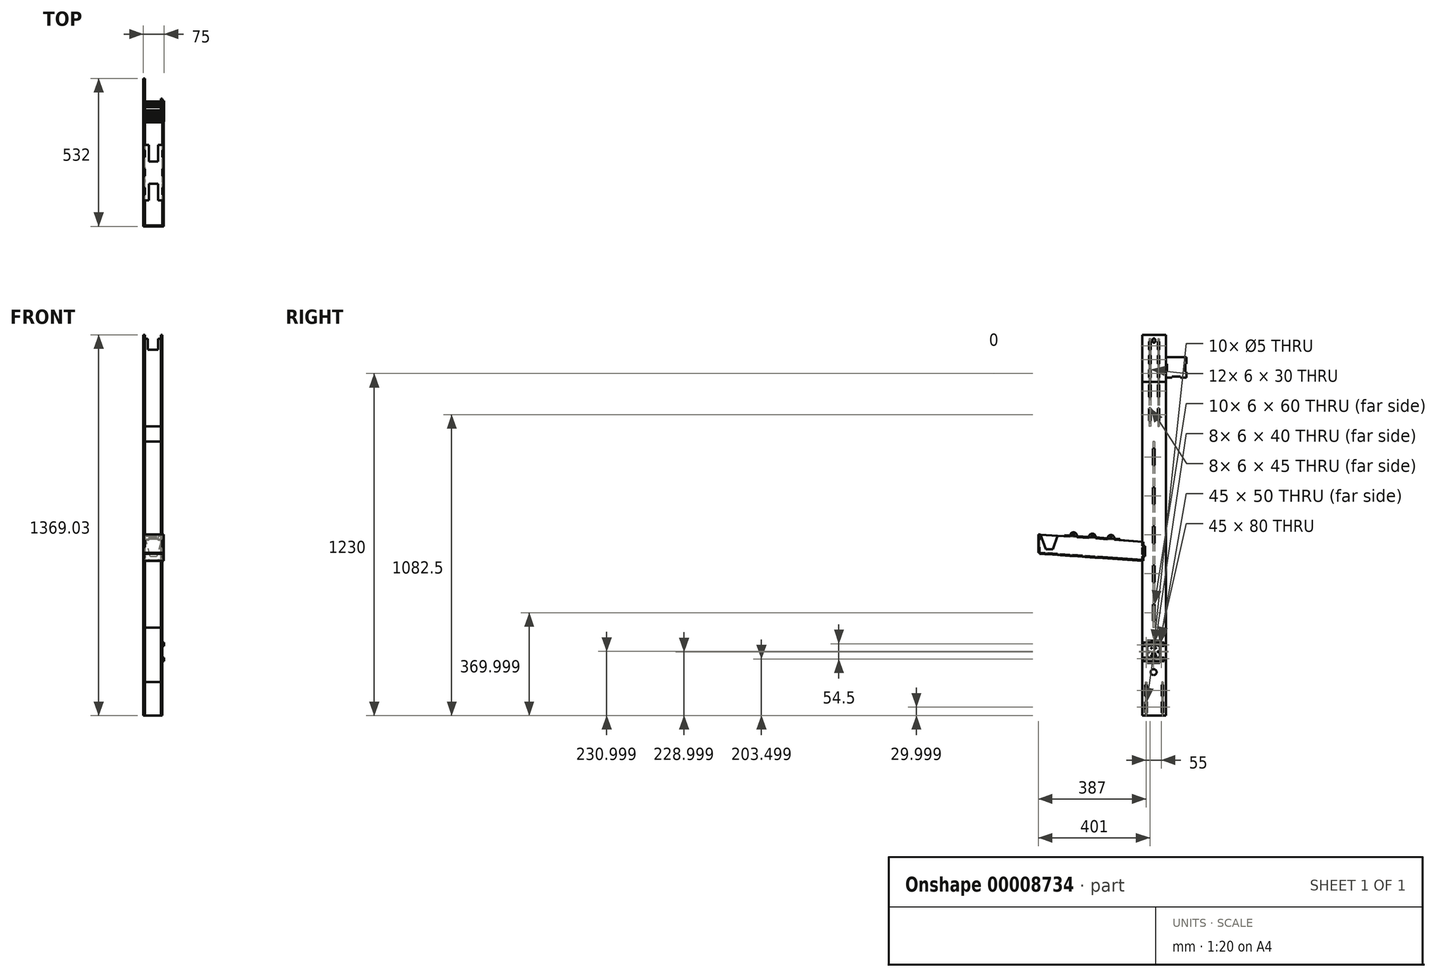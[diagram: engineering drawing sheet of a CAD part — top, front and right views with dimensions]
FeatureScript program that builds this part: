
annotation { "Feature Type Name" : "Feature", "Feature Type Description" : "" }
export const myFeature = defineFeature(function(context is Context, id is Id, definition is map)
    precondition{}
    {
        {
            var Q0;
            Q0=qCreatedBy(makeId("Right.planeOp"),FACE);
            cPlane(context, id + "F0", {"entities" : qUnion([Q0]), "cplaneType" : CPlaneType.OFFSET, "offset" : (65 / 2) * mm, "width" : 150 * mm, "height" : 150 * mm});
        }
        {
            var Q0;
            Q0=qCreatedBy(id+"F0.planeOp",FACE);
            var sketch = newSketch(context, id + "F1", { "sketchPlane" : qUnion([Q0])});
            skLineSegment(sketch, "E0", {"start": v(0, 0) * mm, "end": v(0, 0) * mm});
            skLineSegment(sketch, "E1", {"start": v(0, 65.16) * mm, "end": v(109.73, 57.49) * mm});
            skLineSegment(sketch, "E2", {"start": v(0, 0) * mm, "end": v(19.95, -1.4) * mm});
            skLineSegment(sketch, "E3", {"start": v(370, 39.29) * mm, "end": v(269.34, 46.32) * mm});
            skLineSegment(sketch, "E4", {"start": v(209.49, -14.65) * mm, "end": v(370, -25.87) * mm});
            skCircle(sketch, "E5", {"center": v(34, 62.78) * mm, "radius": 30 * mm, "construction": true});
            skLineSegment(sketch, "E6", {"start": v(64, 65.16) * mm, "end": v(64, -4.48) * mm, "construction": true});
            skLineSegment(sketch, "E7", {"start": v(0, 65.16) * mm, "end": v(64, 65.16) * mm, "construction": true});
            skLineSegment(sketch, "E8", {"start": v(0, 45) * mm, "end": v(0, 65.16) * mm});
            skLineSegment(sketch, "E9", {"start": v(0, 0) * mm, "end": v(0, 20) * mm});
            skLineSegment(sketch, "E10", {"start": v(199.51, -13.95) * mm, "end": v(199.23, -17.94) * mm});
            skLineSegment(sketch, "E11", {"start": v(209.2, -18.64) * mm, "end": v(199.23, -17.94) * mm});
            skLineSegment(sketch, "E12", {"start": v(209.2, -18.64) * mm, "end": v(209.49, -14.65) * mm});
            skLineSegment(sketch, "E13", {"start": v(109.73, -7.67) * mm, "end": v(109.45, -11.66) * mm});
            skLineSegment(sketch, "E14", {"start": v(109.45, -11.66) * mm, "end": v(119.43, -12.36) * mm});
            skLineSegment(sketch, "E15", {"start": v(119.43, -12.36) * mm, "end": v(119.7, -8.37) * mm});
            skLineSegment(sketch, "E16", {"start": v(164.6, -11.5) * mm, "end": v(164.32, -15.5) * mm});
            skLineSegment(sketch, "E17", {"start": v(164.32, -15.5) * mm, "end": v(154.34, -14.8) * mm});
            skLineSegment(sketch, "E18", {"start": v(154.34, -14.8) * mm, "end": v(154.62, -10.81) * mm});
            skLineSegment(sketch, "E19.trimOffspring", {"start": v(164.6, -11.5) * mm, "end": v(199.51, -13.95) * mm});
            skLineSegment(sketch, "E20.trimOffspring", {"start": v(119.7, -8.37) * mm, "end": v(154.62, -10.81) * mm});
            skLineSegment(sketch, "E21", {"start": v(74.82, -5.23) * mm, "end": v(74.54, -9.22) * mm});
            skLineSegment(sketch, "E22", {"start": v(74.54, -9.22) * mm, "end": v(64.56, -8.52) * mm});
            skLineSegment(sketch, "E23", {"start": v(64.56, -8.52) * mm, "end": v(64.84, -4.53) * mm});
            skLineSegment(sketch, "E24", {"start": v(29.93, -2.1) * mm, "end": v(29.65, -6.08) * mm});
            skLineSegment(sketch, "E25", {"start": v(29.65, -6.08) * mm, "end": v(19.67, -5.39) * mm});
            skLineSegment(sketch, "E26", {"start": v(19.67, -5.39) * mm, "end": v(19.95, -1.4) * mm});
            skLineSegment(sketch, "E27.trimOffspring", {"start": v(74.82, -5.23) * mm, "end": v(109.73, -7.67) * mm});
            skLineSegment(sketch, "E28.trimOffspring", {"start": v(29.93, -2.1) * mm, "end": v(64.84, -4.53) * mm});
            skLineSegment(sketch, "E29", {"start": v(269.34, 46.32) * mm, "end": v(269.62, 50.31) * mm});
            skLineSegment(sketch, "E30", {"start": v(269.62, 50.31) * mm, "end": v(244.68, 52.06) * mm, "construction": true});
            skLineSegment(sketch, "E31", {"start": v(244.68, 52.06) * mm, "end": v(244.4, 48.07) * mm});
            skLineSegment(sketch, "E32", {"start": v(202, 51.03) * mm, "end": v(202.29, 55.02) * mm});
            skLineSegment(sketch, "E33", {"start": v(202.29, 55.02) * mm, "end": v(177.35, 56.77) * mm, "construction": true});
            skLineSegment(sketch, "E34", {"start": v(177.35, 56.77) * mm, "end": v(177.07, 52.78) * mm});
            skLineSegment(sketch, "E35", {"start": v(134.67, 55.74) * mm, "end": v(134.95, 59.73) * mm});
            skLineSegment(sketch, "E36", {"start": v(134.95, 59.73) * mm, "end": v(110.01, 61.48) * mm, "construction": true});
            skLineSegment(sketch, "E37", {"start": v(110.01, 61.48) * mm, "end": v(109.73, 57.49) * mm});
            skLineSegment(sketch, "E38.trimOffspring", {"start": v(202, 51.03) * mm, "end": v(244.4, 48.07) * mm});
            skLineSegment(sketch, "E39.trimOffspring", {"start": v(134.67, 55.74) * mm, "end": v(177.07, 52.78) * mm});
            skArc(sketch, "E40", {"start": v(269.62, 50.31) * mm, "mid": v(258.02, 63.66) * mm, "end": v(244.68, 52.06) * mm});
            skArc(sketch, "E41", {"start": v(202.29, 55.02) * mm, "mid": v(190.69, 68.36) * mm, "end": v(177.35, 56.77) * mm});
            skArc(sketch, "E42", {"start": v(134.95, 59.73) * mm, "mid": v(123.35, 73.07) * mm, "end": v(110.01, 61.48) * mm});
            skLineSegment(sketch, "E43", {"start": v(257.15, 51.19) * mm, "end": v(258.02, 63.66) * mm, "construction": true});
            skLineSegment(sketch, "E44", {"start": v(189.82, 55.9) * mm, "end": v(190.69, 68.36) * mm, "construction": true});
            skLineSegment(sketch, "E45", {"start": v(122.48, 60.6) * mm, "end": v(123.35, 73.07) * mm, "construction": true});
            skCircle(sketch, "E46", {"center": v(190.3, 62.88) * mm, "radius": 3 * mm});
            skCircle(sketch, "E47", {"center": v(122.97, 67.59) * mm, "radius": 3 * mm});
            skLineSegment(sketch, "E48", {"start": v(257.85, 61.16) * mm, "end": v(123.18, 70.58) * mm, "construction": true});
            skCircle(sketch, "E49", {"center": v(257.64, 58.17) * mm, "radius": 3 * mm});
            skLineSegment(sketch, "E50", {"start": v(0, 45) * mm, "end": v(-4, 45) * mm});
            skLineSegment(sketch, "E51", {"start": v(-4, 45) * mm, "end": v(-4, 20) * mm});
            skLineSegment(sketch, "E52", {"start": v(-4, 20) * mm, "end": v(0, 20) * mm});
            skLineSegment(sketch, "E53.bottom", {"start": v(374, -6.87) * mm, "end": v(370, -6.87) * mm});
            skLineSegment(sketch, "E53.top", {"start": v(374, 15.13) * mm, "end": v(370, 15.13) * mm});
            skLineSegment(sketch, "E53.left", {"start": v(374, -6.87) * mm, "end": v(374, 15.13) * mm});
            skLineSegment(sketch, "E53.right", {"start": v(370, -6.87) * mm, "end": v(370, 15.13) * mm});
            skLineSegment(sketch, "E54", {"start": v(455, 614.16) * mm, "end": v(455, -585.84) * mm});
            skLineSegment(sketch, "E55", {"start": v(455, -585.84) * mm, "end": v(370, -585.84) * mm});
            skLineSegment(sketch, "E56", {"start": v(370, -585.84) * mm, "end": v(370, -25.87) * mm});
            skLineSegment(sketch, "E57", {"start": v(455, 614.16) * mm, "end": v(370, 614.16) * mm});
            skLineSegment(sketch, "E58", {"start": v(370, 614.16) * mm, "end": v(370, 39.29) * mm});
            skCircle(sketch, "E59", {"center": v(410.5, -429.84) * mm, "radius": 32.5 * mm, "construction": true});
            skCircle(sketch, "E60", {"center": v(410.5, 765.16) * mm, "radius": 32.5 * mm, "construction": true});
            skCircle(sketch, "E61", {"center": v(410.5, -429.84) * mm, "radius": 10.75 * mm});
            skLineSegment(sketch, "E62.bottom", {"start": v(445, -575.84) * mm, "end": v(439, -575.84) * mm});
            skLineSegment(sketch, "E62.top", {"start": v(445, -535.84) * mm, "end": v(439, -535.84) * mm});
            skLineSegment(sketch, "E62.left", {"start": v(445, -575.84) * mm, "end": v(445, -535.84) * mm});
            skLineSegment(sketch, "E62.right", {"start": v(439, -575.84) * mm, "end": v(439, -535.84) * mm});
            skLineSegment(sketch, "E63.bottom", {"start": v(445, -515.84) * mm, "end": v(439, -515.84) * mm});
            skLineSegment(sketch, "E63.top", {"start": v(445, -475.84) * mm, "end": v(439, -475.84) * mm});
            skLineSegment(sketch, "E63.left", {"start": v(445, -515.84) * mm, "end": v(445, -475.84) * mm});
            skLineSegment(sketch, "E63.right", {"start": v(439, -515.84) * mm, "end": v(439, -475.84) * mm});
            skLineSegment(sketch, "E64.bottom", {"start": v(386, -475.84) * mm, "end": v(380, -475.84) * mm});
            skLineSegment(sketch, "E64.top", {"start": v(386, -515.84) * mm, "end": v(380, -515.84) * mm});
            skLineSegment(sketch, "E64.left", {"start": v(386, -475.84) * mm, "end": v(386, -515.84) * mm});
            skLineSegment(sketch, "E64.right", {"start": v(380, -475.84) * mm, "end": v(380, -515.84) * mm});
            skLineSegment(sketch, "E65.bottom", {"start": v(386, -535.84) * mm, "end": v(380, -535.84) * mm});
            skLineSegment(sketch, "E65.top", {"start": v(386, -575.84) * mm, "end": v(380, -575.84) * mm});
            skLineSegment(sketch, "E65.left", {"start": v(386, -535.84) * mm, "end": v(386, -575.84) * mm});
            skLineSegment(sketch, "E65.right", {"start": v(380, -535.84) * mm, "end": v(380, -575.84) * mm});
            skLineSegment(sketch, "E66.bottom", {"start": v(431, 604.16) * mm, "end": v(425, 604.16) * mm});
            skLineSegment(sketch, "E66.top", {"start": v(431, 559.16) * mm, "end": v(425, 559.16) * mm});
            skLineSegment(sketch, "E66.left", {"start": v(431, 604.16) * mm, "end": v(431, 559.16) * mm});
            skLineSegment(sketch, "E66.right", {"start": v(425, 604.16) * mm, "end": v(425, 559.16) * mm});
            skLineSegment(sketch, "E67.bottom", {"start": v(431, 519.16) * mm, "end": v(425, 519.16) * mm});
            skLineSegment(sketch, "E67.top", {"start": v(431, 474.16) * mm, "end": v(425, 474.16) * mm});
            skLineSegment(sketch, "E67.left", {"start": v(431, 519.16) * mm, "end": v(431, 474.16) * mm});
            skLineSegment(sketch, "E67.right", {"start": v(425, 519.16) * mm, "end": v(425, 474.16) * mm});
            skLineSegment(sketch, "E68.bottom", {"start": v(400, 604.16) * mm, "end": v(394, 604.16) * mm});
            skLineSegment(sketch, "E68.top", {"start": v(400, 559.16) * mm, "end": v(394, 559.16) * mm});
            skLineSegment(sketch, "E68.left", {"start": v(400, 604.16) * mm, "end": v(400, 559.16) * mm});
            skLineSegment(sketch, "E68.right", {"start": v(394, 604.16) * mm, "end": v(394, 559.16) * mm});
            skLineSegment(sketch, "E69.bottom", {"start": v(400, 519.16) * mm, "end": v(394, 519.16) * mm});
            skLineSegment(sketch, "E69.top", {"start": v(400, 474.16) * mm, "end": v(394, 474.16) * mm});
            skLineSegment(sketch, "E69.left", {"start": v(400, 519.16) * mm, "end": v(400, 474.16) * mm});
            skLineSegment(sketch, "E69.right", {"start": v(394, 519.16) * mm, "end": v(394, 474.16) * mm});
            skLineSegment(sketch, "E70", {"start": v(425, 604.16) * mm, "end": v(400, 604.16) * mm, "construction": true});
            skLineSegment(sketch, "E71", {"start": v(412.5, 604.16) * mm, "end": v(412.5, 614.16) * mm, "construction": true});
            skLineSegment(sketch, "E72.bottom", {"start": v(433, -329.84) * mm, "end": v(388, -329.84) * mm});
            skLineSegment(sketch, "E72.top", {"start": v(433, -379.84) * mm, "end": v(388, -379.84) * mm});
            skLineSegment(sketch, "E72.left", {"start": v(433, -329.84) * mm, "end": v(433, -379.84) * mm});
            skLineSegment(sketch, "E72.right", {"start": v(388, -329.84) * mm, "end": v(388, -379.84) * mm});
            skPoint(sketch, "E73", {"position": v(410.5, -329.84) * mm});
            skLineSegment(sketch, "E74.bottom", {"start": v(413.5, -245.84) * mm, "end": v(407.5, -245.84) * mm});
            skLineSegment(sketch, "E74.top", {"start": v(413.5, -185.84) * mm, "end": v(407.5, -185.84) * mm});
            skLineSegment(sketch, "E74.left", {"start": v(413.5, -245.84) * mm, "end": v(413.5, -185.84) * mm});
            skLineSegment(sketch, "E74.right", {"start": v(407.5, -245.84) * mm, "end": v(407.5, -185.84) * mm});
            skLineSegment(sketch, "E75.bottom", {"start": v(413.5, -105.84) * mm, "end": v(407.5, -105.84) * mm});
            skLineSegment(sketch, "E75.top", {"start": v(413.5, -45.84) * mm, "end": v(407.5, -45.84) * mm});
            skLineSegment(sketch, "E75.left", {"start": v(413.5, -105.84) * mm, "end": v(413.5, -45.84) * mm});
            skLineSegment(sketch, "E75.right", {"start": v(407.5, -105.84) * mm, "end": v(407.5, -45.84) * mm});
            skLineSegment(sketch, "E76.bottom", {"start": v(413.5, 34.16) * mm, "end": v(407.5, 34.16) * mm});
            skLineSegment(sketch, "E76.top", {"start": v(413.5, 94.16) * mm, "end": v(407.5, 94.16) * mm});
            skLineSegment(sketch, "E76.left", {"start": v(413.5, 34.16) * mm, "end": v(413.5, 94.16) * mm});
            skLineSegment(sketch, "E76.right", {"start": v(407.5, 34.16) * mm, "end": v(407.5, 94.16) * mm});
            skLineSegment(sketch, "E77.bottom", {"start": v(413.5, 174.16) * mm, "end": v(407.5, 174.16) * mm});
            skLineSegment(sketch, "E77.top", {"start": v(413.5, 234.16) * mm, "end": v(407.5, 234.16) * mm});
            skLineSegment(sketch, "E77.left", {"start": v(413.5, 174.16) * mm, "end": v(413.5, 234.16) * mm});
            skLineSegment(sketch, "E77.right", {"start": v(407.5, 174.16) * mm, "end": v(407.5, 234.16) * mm});
            skLineSegment(sketch, "E78.bottom", {"start": v(413.5, 314.16) * mm, "end": v(407.5, 314.16) * mm});
            skLineSegment(sketch, "E78.top", {"start": v(413.5, 374.16) * mm, "end": v(407.5, 374.16) * mm});
            skLineSegment(sketch, "E78.left", {"start": v(413.5, 314.16) * mm, "end": v(413.5, 374.16) * mm});
            skLineSegment(sketch, "E78.right", {"start": v(407.5, 314.16) * mm, "end": v(407.5, 374.16) * mm});
            skLineSegment(sketch, "E79", {"start": v(413.5, -185.84) * mm, "end": v(413.5, -105.84) * mm, "construction": true});
            skLineSegment(sketch, "E80", {"start": v(413.5, -45.84) * mm, "end": v(413.5, 34.16) * mm, "construction": true});
            skLineSegment(sketch, "E81", {"start": v(413.5, 94.16) * mm, "end": v(413.5, 174.16) * mm, "construction": true});
            skLineSegment(sketch, "E82", {"start": v(413.5, 314.16) * mm, "end": v(413.5, 234.16) * mm, "construction": true});
            skPoint(sketch, "E83", {"position": v(410.5, -245.84) * mm});
            skSolve(sketch);
        }
        {
            var Q0;
            Q0 = qSketchRegion(id + "F1", true);
            extrude(context, id + "F2", {"entities" : qUnion([Q0]), "depth" : 4 * mm, "hasSecondDirection" : true, "secondDirectionOppositeDirection" : true, "secondDirectionDepth" : 2 * mm});
        }
        {
            var Q0;
            Q0=makeQuery(id+"F2.opExtrude","SWEPT_FACE",FACE,{"disambiguationData":[OSD([sQuery(id+"F1.wireOp",EDGE,"E2")])]});
            var sketch = newSketch(context, id + "F3", { "sketchPlane" : qUnion([Q0])});
            skLineSegment(sketch, "E84.bottom", {"start": v(30.5, 0) * mm, "end": v(103.5, 0) * mm});
            skLineSegment(sketch, "E84.top", {"start": v(30.5, -370.91) * mm, "end": v(47.5, -370.91) * mm});
            skLineSegment(sketch, "E84.left", {"start": v(30.5, 0) * mm, "end": v(30.5, -20) * mm});
            skLineSegment(sketch, "E84.right", {"start": v(103.5, 0) * mm, "end": v(103.5, -20) * mm});
            skLineSegment(sketch, "E85", {"start": v(88.5, -370.91) * mm, "end": v(88.5, -374.91) * mm});
            skLineSegment(sketch, "E86", {"start": v(47.5, -374.91) * mm, "end": v(47.5, -370.91) * mm});
            skLineSegment(sketch, "E87", {"start": v(82.5, -370.91) * mm, "end": v(82.5, -374.91) * mm});
            skLineSegment(sketch, "E88", {"start": v(53.5, -374.91) * mm, "end": v(53.5, -370.91) * mm});
            skLineSegment(sketch, "E89.trimOffspring", {"start": v(88.5, -370.91) * mm, "end": v(103.5, -370.91) * mm});
            skLineSegment(sketch, "E90.trimOffspring", {"start": v(53.5, -370.91) * mm, "end": v(82.5, -370.91) * mm});
            skLineSegment(sketch, "E91.0.1", {"start": v(30.5, -30) * mm, "end": v(36.5, -30) * mm});
            skLineSegment(sketch, "E91.0.2", {"start": v(36.5, -30) * mm, "end": v(36.5, -20) * mm});
            skLineSegment(sketch, "E91.0.3", {"start": v(36.5, -20) * mm, "end": v(30.5, -20) * mm});
            skLineSegment(sketch, "E91.1.1", {"start": v(30.5, -75) * mm, "end": v(36.5, -75) * mm});
            skLineSegment(sketch, "E91.1.2", {"start": v(36.5, -75) * mm, "end": v(36.5, -65) * mm});
            skLineSegment(sketch, "E91.1.3", {"start": v(36.5, -65) * mm, "end": v(30.5, -65) * mm});
            skLineSegment(sketch, "E91.2.1", {"start": v(30.5, -120) * mm, "end": v(36.5, -120) * mm});
            skLineSegment(sketch, "E91.2.2", {"start": v(36.5, -120) * mm, "end": v(36.5, -110) * mm});
            skLineSegment(sketch, "E91.2.3", {"start": v(36.5, -110) * mm, "end": v(30.5, -110) * mm});
            skLineSegment(sketch, "E91.3.1", {"start": v(30.5, -210) * mm, "end": v(36.5, -210) * mm});
            skLineSegment(sketch, "E91.3.2", {"start": v(36.5, -210) * mm, "end": v(36.5, -200) * mm});
            skLineSegment(sketch, "E91.3.3", {"start": v(36.5, -200) * mm, "end": v(30.5, -200) * mm});
            skLineSegment(sketch, "E91.4.1", {"start": v(30.5, -165) * mm, "end": v(36.5, -165) * mm});
            skLineSegment(sketch, "E91.4.2", {"start": v(36.5, -165) * mm, "end": v(36.5, -155) * mm});
            skLineSegment(sketch, "E91.4.3", {"start": v(36.5, -155) * mm, "end": v(30.5, -155) * mm});
            skLineSegment(sketch, "E92.trimOffspring", {"start": v(30.5, -165) * mm, "end": v(30.5, -200) * mm});
            skLineSegment(sketch, "E93.trimOffspring", {"start": v(30.5, -210) * mm, "end": v(30.5, -370.91) * mm});
            skLineSegment(sketch, "E94.trimOffspring", {"start": v(30.5, -120) * mm, "end": v(30.5, -155) * mm});
            skLineSegment(sketch, "E95.trimOffspring", {"start": v(30.5, -75) * mm, "end": v(30.5, -110) * mm});
            skLineSegment(sketch, "E96.trimOffspring", {"start": v(30.5, -30) * mm, "end": v(30.5, -65) * mm});
            skLineSegment(sketch, "E97.bottom", {"start": v(103.5, -20) * mm, "end": v(99.5, -20) * mm});
            skLineSegment(sketch, "E97.top", {"start": v(103.5, -30) * mm, "end": v(99.5, -30) * mm});
            skLineSegment(sketch, "E97.right", {"start": v(99.5, -20) * mm, "end": v(99.5, -30) * mm});
            skLineSegment(sketch, "E98.bottom", {"start": v(103.5, -65) * mm, "end": v(99.5, -65) * mm});
            skLineSegment(sketch, "E98.top", {"start": v(103.5, -75) * mm, "end": v(99.5, -75) * mm});
            skLineSegment(sketch, "E98.right", {"start": v(99.5, -65) * mm, "end": v(99.5, -75) * mm});
            skLineSegment(sketch, "E99.bottom", {"start": v(103.5, -110) * mm, "end": v(99.5, -110) * mm});
            skLineSegment(sketch, "E99.top", {"start": v(103.5, -120) * mm, "end": v(99.5, -120) * mm});
            skLineSegment(sketch, "E99.right", {"start": v(99.5, -110) * mm, "end": v(99.5, -120) * mm});
            skLineSegment(sketch, "E100.bottom", {"start": v(103.5, -155) * mm, "end": v(99.5, -155) * mm});
            skLineSegment(sketch, "E100.top", {"start": v(103.5, -165) * mm, "end": v(99.5, -165) * mm});
            skLineSegment(sketch, "E100.right", {"start": v(99.5, -155) * mm, "end": v(99.5, -165) * mm});
            skLineSegment(sketch, "E101.bottom", {"start": v(103.5, -200) * mm, "end": v(99.5, -200) * mm});
            skLineSegment(sketch, "E101.top", {"start": v(103.5, -210) * mm, "end": v(99.5, -210) * mm});
            skLineSegment(sketch, "E101.right", {"start": v(99.5, -200) * mm, "end": v(99.5, -210) * mm});
            skLineSegment(sketch, "E102.trimOffspring", {"start": v(103.5, -210) * mm, "end": v(103.5, -370.91) * mm});
            skLineSegment(sketch, "E103.trimOffspring", {"start": v(103.5, -165) * mm, "end": v(103.5, -200) * mm});
            skLineSegment(sketch, "E104.trimOffspring", {"start": v(103.5, -120) * mm, "end": v(103.5, -155) * mm});
            skLineSegment(sketch, "E105.trimOffspring", {"start": v(103.5, -75) * mm, "end": v(103.5, -110) * mm});
            skLineSegment(sketch, "E106.trimOffspring", {"start": v(103.5, -30) * mm, "end": v(103.5, -65) * mm});
            skLineSegment(sketch, "E107", {"start": v(82.5, -374.91) * mm, "end": v(88.5, -374.91) * mm});
            skLineSegment(sketch, "E108", {"start": v(47.5, -374.91) * mm, "end": v(53.5, -374.91) * mm});
            skSolve(sketch);
        }
        {
            var Q0;
            Q0 = qSketchRegion(id + "F3", true);
            extrude(context, id + "F4", {"entities" : qUnion([Q0]), "depth" : 4 * mm});
        }
        {
            var Q0;
            Q0=makeQuery(id+"F2.opExtrude","SWEPT_FACE",FACE,{"disambiguationData":[OSD([sQuery(id+"F1.wireOp",EDGE,"E9")])]});
            var sketch = newSketch(context, id + "F5", { "sketchPlane" : qUnion([Q0])});
            skLineSegment(sketch, "E109.bottom", {"start": v(30.5, 0) * mm, "end": v(103.5, 0) * mm});
            skLineSegment(sketch, "E109.top", {"start": v(32.5, 65.16) * mm, "end": v(103.5, 65.16) * mm});
            skLineSegment(sketch, "E110.0", {"start": v(36.5, 45) * mm, "end": v(32.5, 45) * mm});
            skLineSegment(sketch, "E110.1", {"start": v(36.5, 45) * mm, "end": v(36.5, 20) * mm});
            skLineSegment(sketch, "E110.2", {"start": v(36.5, 0) * mm, "end": v(30.5, 0) * mm});
            skLineSegment(sketch, "E110.3.1", {"start": v(30.5, 0) * mm, "end": v(36.5, 0) * mm});
            skLineSegment(sketch, "E110.3.2", {"start": v(36.5, 20) * mm, "end": v(36.5, 45) * mm});
            skLineSegment(sketch, "E110.3.3", {"start": v(36.5, 45) * mm, "end": v(32.5, 45) * mm});
            skLineSegment(sketch, "E111.trimOffspring", {"start": v(32.5, 45) * mm, "end": v(32.5, 65.16) * mm});
            skLineSegment(sketch, "E112.trimOffspring", {"start": v(30.5, 0) * mm, "end": v(30.5, 0) * mm});
            skLineSegment(sketch, "E113.bottom", {"start": v(103.5, 45) * mm, "end": v(99.5, 45) * mm});
            skLineSegment(sketch, "E113.top", {"start": v(103.5, 20) * mm, "end": v(99.5, 20) * mm});
            skLineSegment(sketch, "E113.right", {"start": v(99.5, 45) * mm, "end": v(99.5, 20) * mm});
            skLineSegment(sketch, "E114.trimOffspring", {"start": v(103.5, 0) * mm, "end": v(103.5, 20) * mm});
            skLineSegment(sketch, "E115.trimOffspring", {"start": v(103.5, 45) * mm, "end": v(103.5, 65.16) * mm});
            skLineSegment(sketch, "E116", {"start": v(36.5, 20) * mm, "end": v(30.5, 20) * mm});
            skLineSegment(sketch, "E117", {"start": v(30.5, 0) * mm, "end": v(30.5, 20) * mm});
            skSolve(sketch);
        }
        {
            var Q0;
            Q0 = qSketchRegion(id + "F5", true);
            extrude(context, id + "F6", {"entities" : qUnion([Q0]), "depth" : 4 * mm});
        }
        {
            var Q0;
            Q0=makeQuery(id+"F4.opExtrude","SWEPT_FACE",FACE,{"disambiguationData":[OSD([sQuery(id+"F3.wireOp",EDGE,"E84.right")])]});
            var sketch = newSketch(context, id + "F7", { "sketchPlane" : qUnion([Q0])});
            skLineSegment(sketch, "E118", {"start": v(370, -25.87) * mm, "end": v(370, -12.71) * mm});
            skLineSegment(sketch, "E119", {"start": v(370, 39.29) * mm, "end": v(269.34, 46.32) * mm});
            skLineSegment(sketch, "E120.bottom", {"start": v(370, 24.29) * mm, "end": v(380, 24.29) * mm});
            skLineSegment(sketch, "E120.top", {"start": v(370, -12.71) * mm, "end": v(380, -12.71) * mm});
            skLineSegment(sketch, "E120.right", {"start": v(380, 24.29) * mm, "end": v(380, -12.71) * mm});
            skLineSegment(sketch, "E121", {"start": v(370, 18.29) * mm, "end": v(374, 18.29) * mm});
            skLineSegment(sketch, "E122", {"start": v(374, 18.29) * mm, "end": v(374, -6.71) * mm});
            skLineSegment(sketch, "E123", {"start": v(374, -6.71) * mm, "end": v(370, -6.71) * mm});
            skLineSegment(sketch, "E124.trimOffspring", {"start": v(370, 24.29) * mm, "end": v(370, 39.29) * mm});
            skLineSegment(sketch, "E125.trimOffspring", {"start": v(370, -6.71) * mm, "end": v(370, 18.29) * mm});
            skLineSegment(sketch, "E126", {"start": v(0, 45) * mm, "end": v(-4, 45) * mm});
            skLineSegment(sketch, "E127", {"start": v(-4, 45) * mm, "end": v(-4, 20) * mm});
            skLineSegment(sketch, "E128", {"start": v(-4, 20) * mm, "end": v(0, 20) * mm});
            skLineSegment(sketch, "E129.trimOffspring", {"start": v(0, 0) * mm, "end": v(0, 20) * mm});
            skLineSegment(sketch, "E130.0", {"start": v(29.93, -2.1) * mm, "end": v(29.65, -6.08) * mm});
            skLineSegment(sketch, "E130.1", {"start": v(19.67, -5.39) * mm, "end": v(19.95, -1.4) * mm});
            skLineSegment(sketch, "E130.2", {"start": v(29.65, -6.08) * mm, "end": v(19.67, -5.39) * mm});
            skLineSegment(sketch, "E130.3", {"start": v(64.56, -8.52) * mm, "end": v(64.84, -4.53) * mm});
            skLineSegment(sketch, "E130.4", {"start": v(74.54, -9.22) * mm, "end": v(64.56, -8.52) * mm});
            skLineSegment(sketch, "E130.5", {"start": v(74.82, -5.23) * mm, "end": v(74.54, -9.22) * mm});
            skLineSegment(sketch, "E130.6", {"start": v(109.73, -7.67) * mm, "end": v(109.45, -11.66) * mm});
            skLineSegment(sketch, "E130.7", {"start": v(119.43, -12.36) * mm, "end": v(119.7, -8.37) * mm});
            skLineSegment(sketch, "E130.8", {"start": v(109.45, -11.66) * mm, "end": v(119.43, -12.36) * mm});
            skLineSegment(sketch, "E130.9", {"start": v(74.82, -5.23) * mm, "end": v(109.73, -7.67) * mm});
            skLineSegment(sketch, "E130.10", {"start": v(29.93, -2.1) * mm, "end": v(64.84, -4.53) * mm});
            skLineSegment(sketch, "E130.11", {"start": v(0, 0) * mm, "end": v(19.95, -1.4) * mm});
            skLineSegment(sketch, "E130.12", {"start": v(119.7, -8.37) * mm, "end": v(154.62, -10.81) * mm});
            skLineSegment(sketch, "E130.13", {"start": v(154.34, -14.8) * mm, "end": v(154.62, -10.81) * mm});
            skLineSegment(sketch, "E130.14", {"start": v(164.32, -15.5) * mm, "end": v(154.34, -14.8) * mm});
            skLineSegment(sketch, "E130.15", {"start": v(164.6, -11.5) * mm, "end": v(164.32, -15.5) * mm});
            skLineSegment(sketch, "E130.16", {"start": v(164.6, -11.5) * mm, "end": v(199.51, -13.95) * mm});
            skLineSegment(sketch, "E130.17", {"start": v(199.51, -13.95) * mm, "end": v(199.23, -17.94) * mm});
            skLineSegment(sketch, "E130.18", {"start": v(209.2, -18.64) * mm, "end": v(199.23, -17.94) * mm});
            skLineSegment(sketch, "E130.19", {"start": v(209.2, -18.64) * mm, "end": v(209.49, -14.65) * mm});
            skLineSegment(sketch, "E130.20", {"start": v(209.49, -14.65) * mm, "end": v(370, -25.87) * mm});
            skLineSegment(sketch, "E131", {"start": v(109.73, 57.49) * mm, "end": v(110.01, 61.48) * mm});
            skLineSegment(sketch, "E132", {"start": v(110.01, 61.48) * mm, "end": v(134.95, 59.73) * mm});
            skLineSegment(sketch, "E133", {"start": v(134.95, 59.73) * mm, "end": v(134.67, 55.74) * mm});
            skLineSegment(sketch, "E134.trimOffspring", {"start": v(109.73, 57.49) * mm, "end": v(65.13, 60.6) * mm});
            skLineSegment(sketch, "E135", {"start": v(177.07, 52.78) * mm, "end": v(177.35, 56.77) * mm});
            skLineSegment(sketch, "E136", {"start": v(177.35, 56.77) * mm, "end": v(202.29, 55.02) * mm});
            skLineSegment(sketch, "E137", {"start": v(202.29, 55.02) * mm, "end": v(202, 51.03) * mm});
            skLineSegment(sketch, "E138.trimOffspring", {"start": v(177.07, 52.78) * mm, "end": v(134.67, 55.74) * mm});
            skLineSegment(sketch, "E139", {"start": v(244.4, 48.07) * mm, "end": v(244.68, 52.06) * mm});
            skLineSegment(sketch, "E140", {"start": v(244.68, 52.06) * mm, "end": v(269.62, 50.31) * mm});
            skLineSegment(sketch, "E141", {"start": v(269.62, 50.31) * mm, "end": v(269.34, 46.32) * mm});
            skLineSegment(sketch, "E142.trimOffspring", {"start": v(244.4, 48.07) * mm, "end": v(202, 51.03) * mm});
            skLineSegment(sketch, "E143", {"start": v(0, 65.16) * mm, "end": v(0, 45) * mm});
            skLineSegment(sketch, "E144", {"start": v(4, 64.88) * mm, "end": v(22.96, 12.75) * mm});
            skLineSegment(sketch, "E145", {"start": v(22.96, 12.75) * mm, "end": v(47.71, 12.75) * mm});
            skLineSegment(sketch, "E146", {"start": v(47.71, 12.75) * mm, "end": v(65.13, 60.6) * mm});
            skLineSegment(sketch, "E147.trimOffspring", {"start": v(4, 64.88) * mm, "end": v(0, 65.16) * mm});
            skLineSegment(sketch, "E148", {"start": v(4, 64.88) * mm, "end": v(65.13, 60.6) * mm, "construction": true});
            skLineSegment(sketch, "E149", {"start": v(34.56, 62.74) * mm, "end": v(35.34, 12.75) * mm, "construction": true});
            skSolve(sketch);
        }
        {
            var Q0;
            Q0 = qSketchRegion(id + "F7", true);
            extrude(context, id + "F8", {"entities" : qUnion([Q0]), "oppositeDirection" : true, "depth" : 4 * mm});
        }
        {
            var Q0;
            Q0=makeQuery(id+"F8.opExtrude","SWEPT_FACE",FACE,{"disambiguationData":[OSD([sQuery(id+"F7.wireOp",EDGE,"E118")])]});
            var sketch = newSketch(context, id + "F9", { "sketchPlane" : qUnion([Q0])});
            skLineSegment(sketch, "E150.bottom", {"start": v(-103.5, 39.29) * mm, "end": v(-93.5, 39.29) * mm});
            skLineSegment(sketch, "E150.left", {"start": v(-103.5, 39.29) * mm, "end": v(-103.5, 24.29) * mm});
            skLineSegment(sketch, "E151.bottom", {"start": v(-103.5, 24.29) * mm, "end": v(-99.5, 24.29) * mm});
            skLineSegment(sketch, "E151.top", {"start": v(-103.5, 18.29) * mm, "end": v(-99.5, 18.29) * mm});
            skLineSegment(sketch, "E151.right", {"start": v(-99.5, 24.29) * mm, "end": v(-99.5, 18.29) * mm});
            skLineSegment(sketch, "E152.top", {"start": v(-103.5, -6.71) * mm, "end": v(-99.5, -6.71) * mm});
            skLineSegment(sketch, "E153.trimOffspring", {"start": v(-103.5, 18.29) * mm, "end": v(-103.5, -6.71) * mm});
            skLineSegment(sketch, "E154.trimOffspring", {"start": v(-41.5, 39.29) * mm, "end": v(-36.5, 39.29) * mm});
            skLineSegment(sketch, "E155", {"start": v(-99.5, -6.71) * mm, "end": v(-99.5, -12.71) * mm});
            skLineSegment(sketch, "E156", {"start": v(-99.5, -12.71) * mm, "end": v(-103.5, -12.71) * mm});
            skLineSegment(sketch, "E157", {"start": v(-103.5, -12.71) * mm, "end": v(-103.5, -29.86) * mm});
            skLineSegment(sketch, "E158", {"start": v(-103.5, -29.86) * mm, "end": v(-88.5, -29.86) * mm});
            skLineSegment(sketch, "E159", {"start": v(-88.5, -29.86) * mm, "end": v(-88.5, -25.87) * mm});
            skLineSegment(sketch, "E160", {"start": v(-88.5, -25.87) * mm, "end": v(-82.5, -25.87) * mm});
            skLineSegment(sketch, "E161", {"start": v(-82.5, -25.87) * mm, "end": v(-82.5, -29.86) * mm});
            skLineSegment(sketch, "E162", {"start": v(-82.5, -29.86) * mm, "end": v(-53.5, -29.86) * mm});
            skLineSegment(sketch, "E163", {"start": v(-53.5, -29.86) * mm, "end": v(-53.5, -25.87) * mm});
            skLineSegment(sketch, "E164", {"start": v(-53.5, -25.87) * mm, "end": v(-47.5, -25.87) * mm});
            skLineSegment(sketch, "E165", {"start": v(-47.5, -25.87) * mm, "end": v(-47.5, -29.86) * mm});
            skLineSegment(sketch, "E166", {"start": v(-47.5, -29.86) * mm, "end": v(-36.5, -29.86) * mm});
            skLineSegment(sketch, "E167", {"start": v(-93.5, 39.29) * mm, "end": v(-79, -14.86) * mm});
            skLineSegment(sketch, "E168", {"start": v(-79, -14.86) * mm, "end": v(-56, -14.86) * mm});
            skLineSegment(sketch, "E169", {"start": v(-56, -14.86) * mm, "end": v(-41.5, 39.29) * mm});
            skLineSegment(sketch, "E170", {"start": v(-36.5, 19.13) * mm, "end": v(-36.5, 15.13) * mm});
            skLineSegment(sketch, "E171", {"start": v(-36.5, 15.13) * mm, "end": v(-30.5, 15.13) * mm});
            skLineSegment(sketch, "E172", {"start": v(-30.5, -6.87) * mm, "end": v(-36.5, -6.87) * mm});
            skLineSegment(sketch, "E173", {"start": v(-36.5, -6.87) * mm, "end": v(-36.5, -10.88) * mm});
            skLineSegment(sketch, "E174.trimOffspring", {"start": v(-30.5, 15.13) * mm, "end": v(-30.5, -6.87) * mm});
            skLineSegment(sketch, "E175", {"start": v(-36.5, 19.13) * mm, "end": v(-36.5, 39.29) * mm});
            skLineSegment(sketch, "E176", {"start": v(-36.5, -10.88) * mm, "end": v(-36.5, -29.86) * mm});
            skLineSegment(sketch, "E177.bottom", {"start": v(-99.5, -1.71) * mm, "end": v(-93.5, -1.71) * mm});
            skLineSegment(sketch, "E177.top", {"start": v(-99.5, 13.29) * mm, "end": v(-93.5, 13.29) * mm});
            skLineSegment(sketch, "E177.left", {"start": v(-99.5, -1.71) * mm, "end": v(-99.5, 13.29) * mm});
            skLineSegment(sketch, "E177.right", {"start": v(-93.5, -1.71) * mm, "end": v(-93.5, 13.29) * mm});
            skSolve(sketch);
        }
        {
            var Q0;
            Q0 = qSketchRegion(id + "F9", true);
            extrude(context, id + "F10", {"entities" : qUnion([Q0]), "depth" : 4 * mm});
        }
        {
            var Q0;
            Q0=makeQuery(id+"F2.opExtrude","SWEPT_FACE",FACE,{"disambiguationData":[OSD([sQuery(id+"F1.wireOp",EDGE,"E1")])]});
            var sketch = newSketch(context, id + "F11", { "sketchPlane" : qUnion([Q0])});
            skLineSegment(sketch, "E178.bottom", {"start": v(30.5, 285.45) * mm, "end": v(50.5, 285.45) * mm});
            skLineSegment(sketch, "E178.top", {"start": v(30.5, 85.45) * mm, "end": v(50.5, 85.45) * mm});
            skLineSegment(sketch, "E178.right", {"start": v(103.5, 285.45) * mm, "end": v(103.5, 265.45) * mm});
            skLineSegment(sketch, "E179.top", {"start": v(50.5, 145.45) * mm, "end": v(83.5, 145.45) * mm});
            skLineSegment(sketch, "E179.left", {"start": v(50.5, 85.45) * mm, "end": v(50.5, 145.45) * mm});
            skLineSegment(sketch, "E179.right", {"start": v(83.5, 85.45) * mm, "end": v(83.5, 145.45) * mm});
            skLineSegment(sketch, "E180.top", {"start": v(50.5, 225.45) * mm, "end": v(83.5, 225.45) * mm});
            skLineSegment(sketch, "E180.left", {"start": v(50.5, 285.45) * mm, "end": v(50.5, 225.45) * mm});
            skLineSegment(sketch, "E180.right", {"start": v(83.5, 285.45) * mm, "end": v(83.5, 225.45) * mm});
            skLineSegment(sketch, "E181.trimOffspring", {"start": v(83.5, 85.45) * mm, "end": v(103.5, 85.45) * mm});
            skLineSegment(sketch, "E182.trimOffspring", {"start": v(83.5, 285.45) * mm, "end": v(103.5, 285.45) * mm});
            skLineSegment(sketch, "E183.bottom", {"start": v(30.5, 105.45) * mm, "end": v(36.5, 105.45) * mm});
            skLineSegment(sketch, "E183.top", {"start": v(30.5, 130.45) * mm, "end": v(36.5, 130.45) * mm});
            skLineSegment(sketch, "E183.right", {"start": v(36.5, 105.45) * mm, "end": v(36.5, 130.45) * mm});
            skLineSegment(sketch, "E184.bottom", {"start": v(103.5, 105.45) * mm, "end": v(99.5, 105.45) * mm});
            skLineSegment(sketch, "E184.top", {"start": v(103.5, 130.45) * mm, "end": v(99.5, 130.45) * mm});
            skLineSegment(sketch, "E184.right", {"start": v(99.5, 105.45) * mm, "end": v(99.5, 130.45) * mm});
            skLineSegment(sketch, "E185.bottom", {"start": v(36.5, 172.95) * mm, "end": v(30.5, 172.95) * mm});
            skLineSegment(sketch, "E185.top", {"start": v(36.5, 197.95) * mm, "end": v(30.5, 197.95) * mm});
            skLineSegment(sketch, "E185.left", {"start": v(36.5, 172.95) * mm, "end": v(36.5, 197.95) * mm});
            skLineSegment(sketch, "E186.bottom", {"start": v(30.5, 240.45) * mm, "end": v(36.5, 240.45) * mm});
            skLineSegment(sketch, "E186.top", {"start": v(30.5, 265.45) * mm, "end": v(36.5, 265.45) * mm});
            skLineSegment(sketch, "E186.right", {"start": v(36.5, 240.45) * mm, "end": v(36.5, 265.45) * mm});
            skLineSegment(sketch, "E187.bottom", {"start": v(99.5, 240.45) * mm, "end": v(103.5, 240.45) * mm});
            skLineSegment(sketch, "E187.top", {"start": v(99.5, 265.45) * mm, "end": v(103.5, 265.45) * mm});
            skLineSegment(sketch, "E187.left", {"start": v(99.5, 240.45) * mm, "end": v(99.5, 265.45) * mm});
            skLineSegment(sketch, "E188.bottom", {"start": v(99.5, 172.95) * mm, "end": v(103.5, 172.95) * mm});
            skLineSegment(sketch, "E188.top", {"start": v(99.5, 197.95) * mm, "end": v(103.5, 197.95) * mm});
            skLineSegment(sketch, "E188.left", {"start": v(99.5, 172.95) * mm, "end": v(99.5, 197.95) * mm});
            skLineSegment(sketch, "E189", {"start": v(36.5, 185.45) * mm, "end": v(99.5, 185.45) * mm, "construction": true});
            skLineSegment(sketch, "E190.trimOffspring", {"start": v(103.5, 105.45) * mm, "end": v(103.5, 85.45) * mm});
            skLineSegment(sketch, "E191.trimOffspring", {"start": v(103.5, 172.95) * mm, "end": v(103.5, 130.45) * mm});
            skLineSegment(sketch, "E192.trimOffspring", {"start": v(103.5, 240.45) * mm, "end": v(103.5, 197.95) * mm});
            skLineSegment(sketch, "E193.trimOffspring", {"start": v(30.5, 172.95) * mm, "end": v(30.5, 130.45) * mm});
            skLineSegment(sketch, "E194.trimOffspring", {"start": v(30.5, 105.45) * mm, "end": v(30.5, 85.45) * mm});
            skLineSegment(sketch, "E195", {"start": v(30.5, 240.45) * mm, "end": v(30.5, 197.95) * mm});
            skLineSegment(sketch, "E196", {"start": v(30.5, 265.45) * mm, "end": v(30.5, 285.45) * mm});
            skSolve(sketch);
        }
        {
            var Q0;
            Q0 = qSketchRegion(id + "F11", true);
            extrude(context, id + "F12", {"entities" : qUnion([Q0]), "depth" : 4 * mm});
        }
        {
            var Q0;
            Q0=makeQuery(id+"F2.opExtrude","CAP_FACE",FACE,{"disambiguationData":[OSD([sQuery(id+"F1.wireOp",EDGE,"E1"),sQuery(id+"F1.wireOp",EDGE,"E2"),sQuery(id+"F1.wireOp",EDGE,"E3"),sQuery(id+"F1.wireOp",EDGE,"E4"),sQuery(id+"F1.wireOp",EDGE,"E8"),sQuery(id+"F1.wireOp",EDGE,"E9"),sQuery(id+"F1.wireOp",EDGE,"E10"),sQuery(id+"F1.wireOp",EDGE,"E11"),sQuery(id+"F1.wireOp",EDGE,"E12"),sQuery(id+"F1.wireOp",EDGE,"2ea860bb-12e6-4d5b-9610-7bef03a5f5ce.trimOffspring"),sQuery(id+"F1.wireOp",EDGE,"E13"),sQuery(id+"F1.wireOp",EDGE,"E14"),sQuery(id+"F1.wireOp",EDGE,"E15"),sQuery(id+"F1.wireOp",EDGE,"E16"),sQuery(id+"F1.wireOp",EDGE,"E17"),sQuery(id+"F1.wireOp",EDGE,"E18"),sQuery(id+"F1.wireOp",EDGE,"E19.trimOffspring"),sQuery(id+"F1.wireOp",EDGE,"E20.trimOffspring"),sQuery(id+"F1.wireOp",EDGE,"E21"),sQuery(id+"F1.wireOp",EDGE,"E22"),sQuery(id+"F1.wireOp",EDGE,"E23"),sQuery(id+"F1.wireOp",EDGE,"E24"),sQuery(id+"F1.wireOp",EDGE,"E25"),sQuery(id+"F1.wireOp",EDGE,"E26"),sQuery(id+"F1.wireOp",EDGE,"E27.trimOffspring"),sQuery(id+"F1.wireOp",EDGE,"E28.trimOffspring"),sQuery(id+"F1.wireOp",EDGE,"E29"),sQuery(id+"F1.wireOp",EDGE,"E31"),sQuery(id+"F1.wireOp",EDGE,"E32"),sQuery(id+"F1.wireOp",EDGE,"E34"),sQuery(id+"F1.wireOp",EDGE,"E35"),sQuery(id+"F1.wireOp",EDGE,"E37"),sQuery(id+"F1.wireOp",EDGE,"de55c738-db85-4cea-87b7-ee02274e565e.trimOffspring"),sQuery(id+"F1.wireOp",EDGE,"E38.trimOffspring"),sQuery(id+"F1.wireOp",EDGE,"E39.trimOffspring"),sQuery(id+"F1.wireOp",EDGE,"E40"),sQuery(id+"F1.wireOp",EDGE,"E41"),sQuery(id+"F1.wireOp",EDGE,"E42"),sQuery(id+"F1.wireOp",EDGE,"E46"),sQuery(id+"F1.wireOp",EDGE,"E47"),sQuery(id+"F1.wireOp",EDGE,"E49"),sQuery(id+"F1.wireOp",EDGE,"E50"),sQuery(id+"F1.wireOp",EDGE,"E51"),sQuery(id+"F1.wireOp",EDGE,"E52"),sQuery(id+"F1.wireOp",EDGE,"E53.bottom"),sQuery(id+"F1.wireOp",EDGE,"E53.top"),sQuery(id+"F1.wireOp",EDGE,"E53.left"),sQuery(id+"F1.wireOp",EDGE,"E53.right"),sQuery(id+"F1.wireOp",EDGE,"E54"),sQuery(id+"F1.wireOp",EDGE,"E55"),sQuery(id+"F1.wireOp",EDGE,"E56"),sQuery(id+"F1.wireOp",EDGE,"E57"),sQuery(id+"F1.wireOp",EDGE,"E58")])],"isStart":true});
            cPlane(context, id + "F13", {"entities" : qUnion([Q0]), "cplaneType" : CPlaneType.OFFSET, "offset" : 67 * mm, "oppositeDirection" : true, "width" : 150 * mm, "height" : 150 * mm});
        }
        {
            var Q0;
            Q0=qCreatedBy(id+"F13.planeOp",FACE);
            var sketch = newSketch(context, id + "F14", { "sketchPlane" : qUnion([Q0])});
            skLineSegment(sketch, "E197.bottom", {"start": v(-455, -585.84) * mm, "end": v(-370, -585.84) * mm});
            skLineSegment(sketch, "E197.top", {"start": v(-455, 614.16) * mm, "end": v(-370, 614.16) * mm});
            skLineSegment(sketch, "E197.left", {"start": v(-370, -585.84) * mm, "end": v(-370, -29.86) * mm});
            skLineSegment(sketch, "E197.right", {"start": v(-455, -585.84) * mm, "end": v(-455, 614.16) * mm});
            skLineSegment(sketch, "E198", {"start": v(-370, 39.29) * mm, "end": v(-374, 39.29) * mm});
            skLineSegment(sketch, "E199", {"start": v(-374, 39.29) * mm, "end": v(-374, 13.29) * mm});
            skLineSegment(sketch, "E200", {"start": v(-374, 13.29) * mm, "end": v(-370, 13.29) * mm});
            skLineSegment(sketch, "E201.trimOffspring", {"start": v(-370, 39.29) * mm, "end": v(-370, 614.16) * mm});
            skLineSegment(sketch, "E202", {"start": v(-370, -1.71) * mm, "end": v(-374, -1.71) * mm});
            skLineSegment(sketch, "E203", {"start": v(-374, -1.71) * mm, "end": v(-374, -29.86) * mm});
            skLineSegment(sketch, "E204", {"start": v(-374, -29.86) * mm, "end": v(-370, -29.86) * mm});
            skLineSegment(sketch, "E205.trimOffspring", {"start": v(-370, -1.71) * mm, "end": v(-370, 13.29) * mm});
            skCircle(sketch, "E206.0", {"center": v(-410.5, -429.84) * mm, "radius": 10.75 * mm});
            skLineSegment(sketch, "E207.bottom", {"start": v(-380, -575.84) * mm, "end": v(-386, -575.84) * mm});
            skLineSegment(sketch, "E207.top", {"start": v(-380, -535.84) * mm, "end": v(-386, -535.84) * mm});
            skLineSegment(sketch, "E207.left", {"start": v(-380, -575.84) * mm, "end": v(-380, -535.84) * mm});
            skLineSegment(sketch, "E207.right", {"start": v(-386, -575.84) * mm, "end": v(-386, -535.84) * mm});
            skLineSegment(sketch, "E208.bottom", {"start": v(-380, -515.84) * mm, "end": v(-386, -515.84) * mm});
            skLineSegment(sketch, "E208.top", {"start": v(-380, -475.84) * mm, "end": v(-386, -475.84) * mm});
            skLineSegment(sketch, "E208.left", {"start": v(-380, -515.84) * mm, "end": v(-380, -475.84) * mm});
            skLineSegment(sketch, "E208.right", {"start": v(-386, -515.84) * mm, "end": v(-386, -475.84) * mm});
            skLineSegment(sketch, "E209.bottom", {"start": v(-445, -475.84) * mm, "end": v(-439, -475.84) * mm});
            skLineSegment(sketch, "E209.top", {"start": v(-445, -515.84) * mm, "end": v(-439, -515.84) * mm});
            skLineSegment(sketch, "E209.left", {"start": v(-445, -475.84) * mm, "end": v(-445, -515.84) * mm});
            skLineSegment(sketch, "E209.right", {"start": v(-439, -475.84) * mm, "end": v(-439, -515.84) * mm});
            skLineSegment(sketch, "E210.bottom", {"start": v(-445, -535.84) * mm, "end": v(-439, -535.84) * mm});
            skLineSegment(sketch, "E210.top", {"start": v(-445, -575.84) * mm, "end": v(-439, -575.84) * mm});
            skLineSegment(sketch, "E210.left", {"start": v(-445, -535.84) * mm, "end": v(-445, -575.84) * mm});
            skLineSegment(sketch, "E210.right", {"start": v(-439, -535.84) * mm, "end": v(-439, -575.84) * mm});
            skLineSegment(sketch, "E211.0", {"start": v(-431, 604.16) * mm, "end": v(-431, 559.16) * mm});
            skLineSegment(sketch, "E211.1", {"start": v(-425, 604.16) * mm, "end": v(-425, 559.16) * mm});
            skLineSegment(sketch, "E211.2", {"start": v(-431, 604.16) * mm, "end": v(-425, 604.16) * mm});
            skLineSegment(sketch, "E211.3", {"start": v(-400, 604.16) * mm, "end": v(-394, 604.16) * mm});
            skLineSegment(sketch, "E211.4", {"start": v(-400, 604.16) * mm, "end": v(-400, 559.16) * mm});
            skLineSegment(sketch, "E211.5", {"start": v(-394, 604.16) * mm, "end": v(-394, 559.16) * mm});
            skLineSegment(sketch, "E211.6", {"start": v(-400, 559.16) * mm, "end": v(-394, 559.16) * mm});
            skLineSegment(sketch, "E211.7", {"start": v(-431, 559.16) * mm, "end": v(-425, 559.16) * mm});
            skLineSegment(sketch, "E212.0", {"start": v(-400, 519.16) * mm, "end": v(-394, 519.16) * mm});
            skLineSegment(sketch, "E212.1", {"start": v(-394, 519.16) * mm, "end": v(-394, 474.16) * mm});
            skLineSegment(sketch, "E212.2", {"start": v(-400, 519.16) * mm, "end": v(-400, 474.16) * mm});
            skLineSegment(sketch, "E212.3", {"start": v(-400, 474.16) * mm, "end": v(-394, 474.16) * mm});
            skLineSegment(sketch, "E212.4", {"start": v(-431, 519.16) * mm, "end": v(-425, 519.16) * mm});
            skLineSegment(sketch, "E212.5", {"start": v(-431, 519.16) * mm, "end": v(-431, 474.16) * mm});
            skLineSegment(sketch, "E212.6", {"start": v(-425, 519.16) * mm, "end": v(-425, 474.16) * mm});
            skLineSegment(sketch, "E212.7", {"start": v(-431, 474.16) * mm, "end": v(-425, 474.16) * mm});
            skCircle(sketch, "E213", {"center": v(-410.5, -356.84) * mm, "radius": 15.5 * mm, "construction": true});
            skCircle(sketch, "E214", {"center": v(-410.5, -363.84) * mm, "radius": 6 * mm, "construction": true});
            skCircle(sketch, "E215", {"center": v(-395, -356.84) * mm, "radius": 1.5 * mm, "construction": true});
            skCircle(sketch, "E216", {"center": v(-426, -356.84) * mm, "radius": 1.5 * mm, "construction": true});
            skCircle(sketch, "E217", {"center": v(-418.25, -343.42) * mm, "radius": 1.5 * mm, "construction": true});
            skCircle(sketch, "E218", {"center": v(-402.75, -343.42) * mm, "radius": 1.5 * mm, "construction": true});
            skCircle(sketch, "E219", {"center": v(-402.75, -370.26) * mm, "radius": 1.5 * mm, "construction": true});
            skCircle(sketch, "E220", {"center": v(-418.25, -370.26) * mm, "radius": 1.5 * mm, "construction": true});
            skLineSegment(sketch, "E221", {"start": v(-410.5, -356.84) * mm, "end": v(-402.75, -343.42) * mm, "construction": true});
            skLineSegment(sketch, "E222", {"start": v(-410.5, -356.84) * mm, "end": v(-395, -356.84) * mm, "construction": true});
            skLineSegment(sketch, "E223", {"start": v(-410.5, -356.84) * mm, "end": v(-402.75, -370.26) * mm, "construction": true});
            skLineSegment(sketch, "E224", {"start": v(-410.5, -429.84) * mm, "end": v(-410.5, -356.84) * mm, "construction": true});
            skLineSegment(sketch, "E225.bottom", {"start": v(-388, -316.84) * mm, "end": v(-433, -316.84) * mm});
            skLineSegment(sketch, "E225.top", {"start": v(-388, -396.84) * mm, "end": v(-433, -396.84) * mm});
            skLineSegment(sketch, "E225.left", {"start": v(-388, -316.84) * mm, "end": v(-388, -396.84) * mm});
            skLineSegment(sketch, "E225.right", {"start": v(-433, -316.84) * mm, "end": v(-433, -396.84) * mm});
            skPoint(sketch, "E226", {"position": v(-410.5, -396.84) * mm});
            skCircle(sketch, "E227", {"center": v(-383, -332.1) * mm, "radius": 2.5 * mm});
            skCircle(sketch, "E228", {"center": v(-438, -332.1) * mm, "radius": 2.5 * mm});
            skCircle(sketch, "E229", {"center": v(-383, -381.6) * mm, "radius": 2.5 * mm});
            skCircle(sketch, "E230", {"center": v(-438, -381.6) * mm, "radius": 2.5 * mm});
            skCircle(sketch, "E231", {"center": v(-410.5, -356.84) * mm, "radius": 18.5 * mm, "construction": true});
            skLineSegment(sketch, "E232.0", {"start": v(-413.5, 314.16) * mm, "end": v(-413.5, 374.16) * mm});
            skLineSegment(sketch, "E232.1", {"start": v(-407.5, 314.16) * mm, "end": v(-407.5, 374.16) * mm});
            skLineSegment(sketch, "E232.2", {"start": v(-413.5, 374.16) * mm, "end": v(-407.5, 374.16) * mm});
            skLineSegment(sketch, "E232.3", {"start": v(-413.5, 314.16) * mm, "end": v(-407.5, 314.16) * mm});
            skLineSegment(sketch, "E232.4", {"start": v(-413.5, 174.16) * mm, "end": v(-413.5, 234.16) * mm});
            skLineSegment(sketch, "E232.5", {"start": v(-413.5, 234.16) * mm, "end": v(-407.5, 234.16) * mm});
            skLineSegment(sketch, "E232.6", {"start": v(-407.5, 174.16) * mm, "end": v(-407.5, 234.16) * mm});
            skLineSegment(sketch, "E232.7", {"start": v(-413.5, 174.16) * mm, "end": v(-407.5, 174.16) * mm});
            skLineSegment(sketch, "E232.8", {"start": v(-413.5, 94.16) * mm, "end": v(-407.5, 94.16) * mm});
            skLineSegment(sketch, "E232.9", {"start": v(-413.5, 34.16) * mm, "end": v(-413.5, 94.16) * mm});
            skLineSegment(sketch, "E232.10", {"start": v(-407.5, 34.16) * mm, "end": v(-407.5, 94.16) * mm});
            skLineSegment(sketch, "E232.11", {"start": v(-413.5, 34.16) * mm, "end": v(-407.5, 34.16) * mm});
            skLineSegment(sketch, "E232.12", {"start": v(-413.5, -105.84) * mm, "end": v(-413.5, -45.84) * mm});
            skLineSegment(sketch, "E232.13", {"start": v(-413.5, -45.84) * mm, "end": v(-407.5, -45.84) * mm});
            skLineSegment(sketch, "E232.14", {"start": v(-407.5, -105.84) * mm, "end": v(-407.5, -45.84) * mm});
            skLineSegment(sketch, "E232.15", {"start": v(-413.5, -105.84) * mm, "end": v(-407.5, -105.84) * mm});
            skLineSegment(sketch, "E232.16", {"start": v(-413.5, -245.84) * mm, "end": v(-413.5, -185.84) * mm});
            skLineSegment(sketch, "E232.17", {"start": v(-413.5, -185.84) * mm, "end": v(-407.5, -185.84) * mm});
            skLineSegment(sketch, "E232.18", {"start": v(-407.5, -245.84) * mm, "end": v(-407.5, -185.84) * mm});
            skLineSegment(sketch, "E232.19", {"start": v(-413.5, -245.84) * mm, "end": v(-407.5, -245.84) * mm});
            skSolve(sketch);
        }
        {
            var Q0;
            Q0 = qSketchRegion(id + "F14", true);
            extrude(context, id + "F15", {"entities" : qUnion([Q0]), "depth" : 4 * mm, "hasSecondDirection" : true, "secondDirectionOppositeDirection" : true, "secondDirectionDepth" : 2 * mm});
        }
        {
            var Q0;
            Q0=makeQuery(id+"F2.opExtrude","CAP_FACE",FACE,{"disambiguationData":[OSD([sQuery(id+"F1.wireOp",EDGE,"E1"),sQuery(id+"F1.wireOp",EDGE,"E2"),sQuery(id+"F1.wireOp",EDGE,"E3"),sQuery(id+"F1.wireOp",EDGE,"E4"),sQuery(id+"F1.wireOp",EDGE,"E8"),sQuery(id+"F1.wireOp",EDGE,"E9"),sQuery(id+"F1.wireOp",EDGE,"E10"),sQuery(id+"F1.wireOp",EDGE,"E11"),sQuery(id+"F1.wireOp",EDGE,"E12"),sQuery(id+"F1.wireOp",EDGE,"2ea860bb-12e6-4d5b-9610-7bef03a5f5ce.trimOffspring"),sQuery(id+"F1.wireOp",EDGE,"E13"),sQuery(id+"F1.wireOp",EDGE,"E14"),sQuery(id+"F1.wireOp",EDGE,"E15"),sQuery(id+"F1.wireOp",EDGE,"E16"),sQuery(id+"F1.wireOp",EDGE,"E17"),sQuery(id+"F1.wireOp",EDGE,"E18"),sQuery(id+"F1.wireOp",EDGE,"E19.trimOffspring"),sQuery(id+"F1.wireOp",EDGE,"E20.trimOffspring"),sQuery(id+"F1.wireOp",EDGE,"E21"),sQuery(id+"F1.wireOp",EDGE,"E22"),sQuery(id+"F1.wireOp",EDGE,"E23"),sQuery(id+"F1.wireOp",EDGE,"E24"),sQuery(id+"F1.wireOp",EDGE,"E25"),sQuery(id+"F1.wireOp",EDGE,"E26"),sQuery(id+"F1.wireOp",EDGE,"E27.trimOffspring"),sQuery(id+"F1.wireOp",EDGE,"E28.trimOffspring"),sQuery(id+"F1.wireOp",EDGE,"E29"),sQuery(id+"F1.wireOp",EDGE,"E31"),sQuery(id+"F1.wireOp",EDGE,"E32"),sQuery(id+"F1.wireOp",EDGE,"E34"),sQuery(id+"F1.wireOp",EDGE,"E35"),sQuery(id+"F1.wireOp",EDGE,"E37"),sQuery(id+"F1.wireOp",EDGE,"de55c738-db85-4cea-87b7-ee02274e565e.trimOffspring"),sQuery(id+"F1.wireOp",EDGE,"E38.trimOffspring"),sQuery(id+"F1.wireOp",EDGE,"E39.trimOffspring"),sQuery(id+"F1.wireOp",EDGE,"E40"),sQuery(id+"F1.wireOp",EDGE,"E41"),sQuery(id+"F1.wireOp",EDGE,"E42"),sQuery(id+"F1.wireOp",EDGE,"E46"),sQuery(id+"F1.wireOp",EDGE,"E47"),sQuery(id+"F1.wireOp",EDGE,"E49"),sQuery(id+"F1.wireOp",EDGE,"E50"),sQuery(id+"F1.wireOp",EDGE,"E51"),sQuery(id+"F1.wireOp",EDGE,"E52"),sQuery(id+"F1.wireOp",EDGE,"E53.bottom"),sQuery(id+"F1.wireOp",EDGE,"E53.top"),sQuery(id+"F1.wireOp",EDGE,"E53.left"),sQuery(id+"F1.wireOp",EDGE,"E53.right"),sQuery(id+"F1.wireOp",EDGE,"E54"),sQuery(id+"F1.wireOp",EDGE,"E55"),sQuery(id+"F1.wireOp",EDGE,"E56"),sQuery(id+"F1.wireOp",EDGE,"E57"),sQuery(id+"F1.wireOp",EDGE,"E58")])],"isStart":false});
            var sketch = newSketch(context, id + "F16", { "sketchPlane" : qUnion([Q0])});
            skLineSegment(sketch, "E233", {"start": v(379, 765.16) * mm, "end": v(379, -419.84) * mm});
            skLineSegment(sketch, "E234", {"start": v(444, 765.16) * mm, "end": v(444, -419.84) * mm});
            skArc(sketch, "E235", {"start": v(444, 765.16) * mm, "mid": v(411.5, 797.66) * mm, "end": v(379, 765.16) * mm});
            skArc(sketch, "E236", {"start": v(379, -419.84) * mm, "mid": v(411.5, -452.34) * mm, "end": v(444, -419.84) * mm});
            skSolve(sketch);
        }
        {
            var Q0;
            {var subQ5=sQuery(id+"F16.wireOp",EDGE,"E236");Q0=makeQuery(id+"F16.imprint","IMPRINT",FACE,{"disambiguationData":[TD([[makeQuery(id+"F16.imprint","IMPRINT",EDGE,{"derivedFrom":subQ5}),1.0]])]});}
            var sketch = newSketch(context, id + "F17", { "sketchPlane" : qUnion([Q0])});
            skLineSegment(sketch, "E237.bottom", {"start": v(455, 614.16) * mm, "end": v(370, 614.16) * mm});
            skLineSegment(sketch, "E237.top", {"start": v(370, 783.19) * mm, "end": v(455, 783.19) * mm});
            skLineSegment(sketch, "E237.left", {"start": v(455, 614.16) * mm, "end": v(455, 629.82) * mm});
            skLineSegment(sketch, "E237.right", {"start": v(370, 614.16) * mm, "end": v(370, 783.19) * mm});
            skLineSegment(sketch, "E238.bottom", {"start": v(431, 759.16) * mm, "end": v(425, 759.16) * mm});
            skLineSegment(sketch, "E238.top", {"start": v(431, 729.16) * mm, "end": v(425, 729.16) * mm});
            skLineSegment(sketch, "E238.left", {"start": v(431, 759.16) * mm, "end": v(431, 729.16) * mm});
            skLineSegment(sketch, "E238.right", {"start": v(425, 759.16) * mm, "end": v(425, 729.16) * mm});
            skLineSegment(sketch, "E239.bottom", {"start": v(431, 709.16) * mm, "end": v(425, 709.16) * mm});
            skLineSegment(sketch, "E239.top", {"start": v(431, 679.16) * mm, "end": v(425, 679.16) * mm});
            skLineSegment(sketch, "E239.left", {"start": v(431, 709.16) * mm, "end": v(431, 679.16) * mm});
            skLineSegment(sketch, "E239.right", {"start": v(425, 709.16) * mm, "end": v(425, 679.16) * mm});
            skLineSegment(sketch, "E240.bottom", {"start": v(431, 659.16) * mm, "end": v(425, 659.16) * mm});
            skLineSegment(sketch, "E240.top", {"start": v(431, 629.16) * mm, "end": v(425, 629.16) * mm});
            skLineSegment(sketch, "E240.left", {"start": v(431, 659.16) * mm, "end": v(431, 629.16) * mm});
            skLineSegment(sketch, "E240.right", {"start": v(425, 659.16) * mm, "end": v(425, 629.16) * mm});
            skLineSegment(sketch, "E241.bottom", {"start": v(400, 759.16) * mm, "end": v(394, 759.16) * mm});
            skLineSegment(sketch, "E241.top", {"start": v(400, 729.16) * mm, "end": v(394, 729.16) * mm});
            skLineSegment(sketch, "E241.left", {"start": v(400, 759.16) * mm, "end": v(400, 729.16) * mm});
            skLineSegment(sketch, "E241.right", {"start": v(394, 759.16) * mm, "end": v(394, 729.16) * mm});
            skLineSegment(sketch, "E242.bottom", {"start": v(400, 709.16) * mm, "end": v(394, 709.16) * mm});
            skLineSegment(sketch, "E242.top", {"start": v(400, 679.16) * mm, "end": v(394, 679.16) * mm});
            skLineSegment(sketch, "E242.left", {"start": v(400, 709.16) * mm, "end": v(400, 679.16) * mm});
            skLineSegment(sketch, "E242.right", {"start": v(394, 709.16) * mm, "end": v(394, 679.16) * mm});
            skLineSegment(sketch, "E243.bottom", {"start": v(400, 659.16) * mm, "end": v(394, 659.16) * mm});
            skLineSegment(sketch, "E243.top", {"start": v(400, 629.16) * mm, "end": v(394, 629.16) * mm});
            skLineSegment(sketch, "E243.left", {"start": v(400, 659.16) * mm, "end": v(400, 629.16) * mm});
            skLineSegment(sketch, "E243.right", {"start": v(394, 659.16) * mm, "end": v(394, 629.16) * mm});
            skCircle(sketch, "E244", {"center": v(411.5, 765.16) * mm, "radius": 32.5 * mm, "construction": true});
            skLineSegment(sketch, "E245", {"start": v(412.5, 759.16) * mm, "end": v(412.5, 614.16) * mm, "construction": true});
            skArc(sketch, "E246", {"start": v(416.5, 765.16) * mm, "mid": v(411.5, 770.16) * mm, "end": v(406.5, 765.16) * mm});
            skLineSegment(sketch, "E247", {"start": v(425, 759.16) * mm, "end": v(400, 759.16) * mm, "construction": true});
            skArc(sketch, "E248", {"start": v(406.5, 760.16) * mm, "mid": v(411.5, 755.16) * mm, "end": v(416.5, 760.16) * mm});
            skLineSegment(sketch, "E249", {"start": v(416.5, 765.16) * mm, "end": v(416.5, 760.16) * mm});
            skLineSegment(sketch, "E250", {"start": v(406.5, 760.16) * mm, "end": v(406.5, 765.16) * mm});
            skLineSegment(sketch, "E251", {"start": v(411.5, 765.16) * mm, "end": v(411.5, 734.16) * mm, "construction": true});
            skLineSegment(sketch, "E252", {"start": v(455, 629.82) * mm, "end": v(476.5, 629.82) * mm});
            skLineSegment(sketch, "E253", {"start": v(476.5, 629.82) * mm, "end": v(476.5, 633.82) * mm});
            skLineSegment(sketch, "E254", {"start": v(476.5, 633.82) * mm, "end": v(506.5, 633.82) * mm});
            skLineSegment(sketch, "E255", {"start": v(506.5, 633.82) * mm, "end": v(506.5, 629.82) * mm});
            skLineSegment(sketch, "E256", {"start": v(506.5, 629.82) * mm, "end": v(528, 629.82) * mm});
            skLineSegment(sketch, "E257", {"start": v(528, 629.82) * mm, "end": v(528, 649.5) * mm});
            skLineSegment(sketch, "E258", {"start": v(528, 649.5) * mm, "end": v(524, 649.5) * mm});
            skLineSegment(sketch, "E259", {"start": v(524, 649.5) * mm, "end": v(524, 679.5) * mm});
            skLineSegment(sketch, "E260", {"start": v(524, 679.5) * mm, "end": v(528, 679.5) * mm});
            skLineSegment(sketch, "E261", {"start": v(528, 679.5) * mm, "end": v(528, 703.19) * mm});
            skLineSegment(sketch, "E262", {"start": v(528, 703.19) * mm, "end": v(455, 703.19) * mm});
            skLineSegment(sketch, "E263", {"start": v(455, 649.5) * mm, "end": v(459, 649.5) * mm});
            skLineSegment(sketch, "E264", {"start": v(459, 649.5) * mm, "end": v(459, 679.5) * mm});
            skLineSegment(sketch, "E265", {"start": v(459, 679.5) * mm, "end": v(455, 679.5) * mm});
            skLineSegment(sketch, "E266.trimOffspring", {"start": v(455, 703.19) * mm, "end": v(455, 783.19) * mm});
            skLineSegment(sketch, "E267.trimOffspring", {"start": v(455, 649.5) * mm, "end": v(455, 679.5) * mm});
            skArc(sketch, "E268", {"start": v(406.5, 765.16) * mm, "mid": v(411.5, 760.16) * mm, "end": v(416.5, 765.16) * mm, "construction": true});
            skSolve(sketch);
        }
        {
            var Q0;
            Q0 = qSketchRegion(id + "F17", true);
            extrude(context, id + "F18", {"entities" : qUnion([Q0]), "oppositeDirection" : true, "depth" : 6 * mm});
        }
        {
            var Q0;
            Q0=makeQuery(id+"F15.opExtrude","CAP_FACE",FACE,{"disambiguationData":[OSD([sQuery(id+"F14.wireOp",EDGE,"E197.bottom"),sQuery(id+"F14.wireOp",EDGE,"E197.top"),sQuery(id+"F14.wireOp",EDGE,"E197.left"),sQuery(id+"F14.wireOp",EDGE,"E197.right"),sQuery(id+"F14.wireOp",EDGE,"E198"),sQuery(id+"F14.wireOp",EDGE,"E199"),sQuery(id+"F14.wireOp",EDGE,"E200"),sQuery(id+"F14.wireOp",EDGE,"E201.trimOffspring"),sQuery(id+"F14.wireOp",EDGE,"E202"),sQuery(id+"F14.wireOp",EDGE,"E203"),sQuery(id+"F14.wireOp",EDGE,"E204"),sQuery(id+"F14.wireOp",EDGE,"E205.trimOffspring"),sQuery(id+"F14.wireOp",EDGE,"E206.0")])],"isStart":false});
            var sketch = newSketch(context, id + "F19", { "sketchPlane" : qUnion([Q0])});
            skLineSegment(sketch, "E269", {"start": v(-370, 783.19) * mm, "end": v(-455, 783.19) * mm});
            skLineSegment(sketch, "E270", {"start": v(-455, 783.19) * mm, "end": v(-455, 614.16) * mm});
            skLineSegment(sketch, "E271", {"start": v(-455, 614.16) * mm, "end": v(-370, 614.16) * mm});
            skLineSegment(sketch, "E272", {"start": v(-370, 614.16) * mm, "end": v(-370, 783.19) * mm});
            skLineSegment(sketch, "E273.bottom", {"start": v(-394, 759.16) * mm, "end": v(-400, 759.16) * mm});
            skLineSegment(sketch, "E273.top", {"start": v(-394, 729.16) * mm, "end": v(-400, 729.16) * mm});
            skLineSegment(sketch, "E273.left", {"start": v(-394, 759.16) * mm, "end": v(-394, 729.16) * mm});
            skLineSegment(sketch, "E273.right", {"start": v(-400, 759.16) * mm, "end": v(-400, 729.16) * mm});
            skLineSegment(sketch, "E274.bottom", {"start": v(-394, 709.16) * mm, "end": v(-400, 709.16) * mm});
            skLineSegment(sketch, "E274.top", {"start": v(-394, 679.16) * mm, "end": v(-400, 679.16) * mm});
            skLineSegment(sketch, "E274.left", {"start": v(-394, 709.16) * mm, "end": v(-394, 679.16) * mm});
            skLineSegment(sketch, "E274.right", {"start": v(-400, 709.16) * mm, "end": v(-400, 679.16) * mm});
            skLineSegment(sketch, "E275.bottom", {"start": v(-394, 659.16) * mm, "end": v(-400, 659.16) * mm});
            skLineSegment(sketch, "E275.top", {"start": v(-394, 629.16) * mm, "end": v(-400, 629.16) * mm});
            skLineSegment(sketch, "E275.left", {"start": v(-394, 659.16) * mm, "end": v(-394, 629.16) * mm});
            skLineSegment(sketch, "E275.right", {"start": v(-400, 659.16) * mm, "end": v(-400, 629.16) * mm});
            skLineSegment(sketch, "E276.bottom", {"start": v(-425, 659.16) * mm, "end": v(-431, 659.16) * mm});
            skLineSegment(sketch, "E276.top", {"start": v(-425, 629.16) * mm, "end": v(-431, 629.16) * mm});
            skLineSegment(sketch, "E276.left", {"start": v(-425, 659.16) * mm, "end": v(-425, 629.16) * mm});
            skLineSegment(sketch, "E276.right", {"start": v(-431, 659.16) * mm, "end": v(-431, 629.16) * mm});
            skLineSegment(sketch, "E277.bottom", {"start": v(-425, 709.16) * mm, "end": v(-431, 709.16) * mm});
            skLineSegment(sketch, "E277.top", {"start": v(-425, 679.16) * mm, "end": v(-431, 679.16) * mm});
            skLineSegment(sketch, "E277.left", {"start": v(-425, 709.16) * mm, "end": v(-425, 679.16) * mm});
            skLineSegment(sketch, "E277.right", {"start": v(-431, 709.16) * mm, "end": v(-431, 679.16) * mm});
            skLineSegment(sketch, "E278.bottom", {"start": v(-425, 759.16) * mm, "end": v(-431, 759.16) * mm});
            skLineSegment(sketch, "E278.top", {"start": v(-425, 729.16) * mm, "end": v(-431, 729.16) * mm});
            skLineSegment(sketch, "E278.left", {"start": v(-425, 759.16) * mm, "end": v(-425, 729.16) * mm});
            skLineSegment(sketch, "E278.right", {"start": v(-431, 759.16) * mm, "end": v(-431, 729.16) * mm});
            skLineSegment(sketch, "E279.0", {"start": v(-406.5, 760.16) * mm, "end": v(-406.5, 765.16) * mm});
            skArc(sketch, "E279.1", {"start": v(-416.5, 765.16) * mm, "mid": v(-411.5, 770.16) * mm, "end": v(-406.5, 765.16) * mm});
            skLineSegment(sketch, "E279.2", {"start": v(-416.5, 765.16) * mm, "end": v(-416.5, 760.16) * mm});
            skArc(sketch, "E279.3", {"start": v(-406.5, 760.16) * mm, "mid": v(-411.5, 755.16) * mm, "end": v(-416.5, 760.16) * mm});
            skSolve(sketch);
        }
        {
            var Q0;
            Q0 = qSketchRegion(id + "F19", true);
            extrude(context, id + "F20", {"entities" : qUnion([Q0]), "oppositeDirection" : true, "depth" : 6 * mm});
        }
        {
            var Q0;
            Q0=makeQuery(id+"F20.opExtrude","SWEPT_FACE",FACE,{"disambiguationData":[OSD([sQuery(id+"F19.wireOp",EDGE,"E276.right")])]});
            var sketch = newSketch(context, id + "F21", { "sketchPlane" : qUnion([Q0])});
            skLineSegment(sketch, "E280", {"start": v(93.5, 769.16) * mm, "end": v(93.5, 759.16) * mm});
            skLineSegment(sketch, "E281", {"start": v(93.5, 759.16) * mm, "end": v(99.5, 759.16) * mm});
            skLineSegment(sketch, "E282", {"start": v(99.5, 759.16) * mm, "end": v(99.5, 729.16) * mm});
            skLineSegment(sketch, "E283", {"start": v(99.5, 729.16) * mm, "end": v(93.5, 729.16) * mm});
            skLineSegment(sketch, "E284", {"start": v(93.5, 729.16) * mm, "end": v(93.5, 709.16) * mm});
            skLineSegment(sketch, "E285", {"start": v(93.5, 709.16) * mm, "end": v(99.5, 709.16) * mm});
            skLineSegment(sketch, "E286", {"start": v(99.5, 709.16) * mm, "end": v(99.5, 679.16) * mm});
            skLineSegment(sketch, "E287", {"start": v(99.5, 679.16) * mm, "end": v(93.5, 679.16) * mm});
            skLineSegment(sketch, "E288", {"start": v(93.5, 679.16) * mm, "end": v(93.5, 659.16) * mm});
            skLineSegment(sketch, "E289", {"start": v(93.5, 659.16) * mm, "end": v(99.5, 659.16) * mm});
            skLineSegment(sketch, "E290", {"start": v(99.5, 659.16) * mm, "end": v(99.5, 629.16) * mm});
            skLineSegment(sketch, "E291", {"start": v(99.5, 629.16) * mm, "end": v(93.5, 629.16) * mm});
            skLineSegment(sketch, "E292", {"start": v(93.5, 629.16) * mm, "end": v(93.5, 604.16) * mm});
            skLineSegment(sketch, "E293", {"start": v(65, 454.16) * mm, "end": v(65, 769.16) * mm, "construction": true});
            skLineSegment(sketch, "E294.0.MirrorCS", {"start": v(36.5, 769.16) * mm, "end": v(36.5, 759.16) * mm});
            skLineSegment(sketch, "E295.0.MirrorCS", {"start": v(36.5, 759.16) * mm, "end": v(30.5, 759.16) * mm});
            skLineSegment(sketch, "E296.0.MirrorCS", {"start": v(30.5, 759.16) * mm, "end": v(30.5, 729.16) * mm});
            skLineSegment(sketch, "E297.0.MirrorCS", {"start": v(30.5, 729.16) * mm, "end": v(36.5, 729.16) * mm});
            skLineSegment(sketch, "E298.0.MirrorCS", {"start": v(36.5, 729.16) * mm, "end": v(36.5, 709.16) * mm});
            skLineSegment(sketch, "E299.0.MirrorCS", {"start": v(36.5, 709.16) * mm, "end": v(30.5, 709.16) * mm});
            skLineSegment(sketch, "E300.0.MirrorCS", {"start": v(30.5, 709.16) * mm, "end": v(30.5, 679.16) * mm});
            skLineSegment(sketch, "E301.0.MirrorCS", {"start": v(30.5, 679.16) * mm, "end": v(36.5, 679.16) * mm});
            skLineSegment(sketch, "E302.0.MirrorCS", {"start": v(36.5, 679.16) * mm, "end": v(36.5, 659.16) * mm});
            skLineSegment(sketch, "E303.0.MirrorCS", {"start": v(36.5, 659.16) * mm, "end": v(30.5, 659.16) * mm});
            skLineSegment(sketch, "E304.0.MirrorCS", {"start": v(30.5, 659.16) * mm, "end": v(30.5, 629.16) * mm});
            skLineSegment(sketch, "E305.0.MirrorCS", {"start": v(30.5, 629.16) * mm, "end": v(36.5, 629.16) * mm});
            skLineSegment(sketch, "E306.0.MirrorCS", {"start": v(36.5, 629.16) * mm, "end": v(36.5, 604.16) * mm});
            skLineSegment(sketch, "E307", {"start": v(93.5, 604.16) * mm, "end": v(99.5, 604.16) * mm});
            skLineSegment(sketch, "E308", {"start": v(99.5, 604.16) * mm, "end": v(99.5, 559.16) * mm});
            skLineSegment(sketch, "E309", {"start": v(99.5, 559.16) * mm, "end": v(93.5, 559.16) * mm});
            skLineSegment(sketch, "E310", {"start": v(93.5, 559.16) * mm, "end": v(93.5, 519.16) * mm});
            skLineSegment(sketch, "E311", {"start": v(93.5, 519.16) * mm, "end": v(99.5, 519.16) * mm});
            skLineSegment(sketch, "E312", {"start": v(99.5, 519.16) * mm, "end": v(99.5, 474.16) * mm});
            skLineSegment(sketch, "E313", {"start": v(99.5, 474.16) * mm, "end": v(93.5, 474.16) * mm});
            skLineSegment(sketch, "E314", {"start": v(93.5, 474.16) * mm, "end": v(93.5, 454.16) * mm});
            skLineSegment(sketch, "E315", {"start": v(93.5, 454.16) * mm, "end": v(65, 454.16) * mm});
            skLineSegment(sketch, "E316.0.MirrorCS", {"start": v(36.5, 604.16) * mm, "end": v(30.5, 604.16) * mm});
            skLineSegment(sketch, "E317.0.MirrorCS", {"start": v(30.5, 604.16) * mm, "end": v(30.5, 559.16) * mm});
            skLineSegment(sketch, "E318.0.MirrorCS", {"start": v(30.5, 559.16) * mm, "end": v(36.5, 559.16) * mm});
            skLineSegment(sketch, "E319.0.MirrorCS", {"start": v(36.5, 559.16) * mm, "end": v(36.5, 519.16) * mm});
            skLineSegment(sketch, "E320.0.MirrorCS", {"start": v(36.5, 519.16) * mm, "end": v(30.5, 519.16) * mm});
            skLineSegment(sketch, "E321.0.MirrorCS", {"start": v(30.5, 519.16) * mm, "end": v(30.5, 474.16) * mm});
            skLineSegment(sketch, "E322.0.MirrorCS", {"start": v(30.5, 474.16) * mm, "end": v(36.5, 474.16) * mm});
            skLineSegment(sketch, "E323.0.MirrorCS", {"start": v(36.5, 474.16) * mm, "end": v(36.5, 454.16) * mm});
            skLineSegment(sketch, "E324.0.MirrorCS", {"start": v(36.5, 454.16) * mm, "end": v(65, 454.16) * mm});
            skLineSegment(sketch, "E325", {"start": v(36.5, 769.16) * mm, "end": v(46.5, 769.16) * mm});
            skLineSegment(sketch, "E326", {"start": v(83.5, 769.16) * mm, "end": v(83.5, 729.16) * mm});
            skLineSegment(sketch, "E327", {"start": v(83.5, 729.16) * mm, "end": v(46.5, 729.16) * mm});
            skLineSegment(sketch, "E328", {"start": v(46.5, 729.16) * mm, "end": v(46.5, 769.16) * mm});
            skLineSegment(sketch, "E329.trimOffspring", {"start": v(83.5, 769.16) * mm, "end": v(93.5, 769.16) * mm});
            skSolve(sketch);
        }
        {
            var Q0;
            Q0 = qSketchRegion(id + "F21", true);
            extrude(context, id + "F22", {"entities" : qUnion([Q0]), "depth" : 6 * mm});
        }
        {
            var Q0;
            Q0=makeQuery(id+"F22.opExtrude","CAP_FACE",FACE,{"disambiguationData":[OSD([sQuery(id+"F21.wireOp",EDGE,"E280"),sQuery(id+"F21.wireOp",EDGE,"E281"),sQuery(id+"F21.wireOp",EDGE,"E282"),sQuery(id+"F21.wireOp",EDGE,"E283"),sQuery(id+"F21.wireOp",EDGE,"E284"),sQuery(id+"F21.wireOp",EDGE,"E285"),sQuery(id+"F21.wireOp",EDGE,"E286"),sQuery(id+"F21.wireOp",EDGE,"E287"),sQuery(id+"F21.wireOp",EDGE,"E288"),sQuery(id+"F21.wireOp",EDGE,"E289"),sQuery(id+"F21.wireOp",EDGE,"E290"),sQuery(id+"F21.wireOp",EDGE,"E291"),sQuery(id+"F21.wireOp",EDGE,"E292"),sQuery(id+"F21.wireOp",EDGE,"E294.0.MirrorCS"),sQuery(id+"F21.wireOp",EDGE,"E295.0.MirrorCS"),sQuery(id+"F21.wireOp",EDGE,"E296.0.MirrorCS"),sQuery(id+"F21.wireOp",EDGE,"E297.0.MirrorCS"),sQuery(id+"F21.wireOp",EDGE,"E298.0.MirrorCS"),sQuery(id+"F21.wireOp",EDGE,"E299.0.MirrorCS"),sQuery(id+"F21.wireOp",EDGE,"E300.0.MirrorCS"),sQuery(id+"F21.wireOp",EDGE,"E301.0.MirrorCS"),sQuery(id+"F21.wireOp",EDGE,"E302.0.MirrorCS"),sQuery(id+"F21.wireOp",EDGE,"E303.0.MirrorCS"),sQuery(id+"F21.wireOp",EDGE,"E304.0.MirrorCS"),sQuery(id+"F21.wireOp",EDGE,"E305.0.MirrorCS"),sQuery(id+"F21.wireOp",EDGE,"E306.0.MirrorCS"),sQuery(id+"F21.wireOp",EDGE,"E307"),sQuery(id+"F21.wireOp",EDGE,"E308"),sQuery(id+"F21.wireOp",EDGE,"E309"),sQuery(id+"F21.wireOp",EDGE,"E310"),sQuery(id+"F21.wireOp",EDGE,"E311"),sQuery(id+"F21.wireOp",EDGE,"E312"),sQuery(id+"F21.wireOp",EDGE,"E313"),sQuery(id+"F21.wireOp",EDGE,"E314"),sQuery(id+"F21.wireOp",EDGE,"E315"),sQuery(id+"F21.wireOp",EDGE,"E316.0.MirrorCS"),sQuery(id+"F21.wireOp",EDGE,"E317.0.MirrorCS"),sQuery(id+"F21.wireOp",EDGE,"E318.0.MirrorCS"),sQuery(id+"F21.wireOp",EDGE,"E319.0.MirrorCS"),sQuery(id+"F21.wireOp",EDGE,"E320.0.MirrorCS"),sQuery(id+"F21.wireOp",EDGE,"E321.0.MirrorCS"),sQuery(id+"F21.wireOp",EDGE,"E322.0.MirrorCS"),sQuery(id+"F21.wireOp",EDGE,"E323.0.MirrorCS"),sQuery(id+"F21.wireOp",EDGE,"E324.0.MirrorCS"),sQuery(id+"F21.wireOp",EDGE,"E325")])],"isStart":false});
            var Q1;
            Q1=makeQuery(id+"F15.opExtrude","SWEPT_FACE",FACE,{"disambiguationData":[OSD([sQuery(id+"F14.wireOp",EDGE,"E211.4")])]});
            cPlane(context, id + "F23", {"entities" : qUnion([Q0, Q1]), "cplaneType" : CPlaneType.MID_PLANE, "offset" : 150 * mm, "width" : 150 * mm, "height" : 150 * mm});
        }
        {
            var Q0;
            Q0=makeQuery(id+"F22.opExtrude","SWEPT_BODY",BODY,{"disambiguationData":[OSD([sQuery(id+"F21.wireOp",EDGE,"f3a64820-0533-4dc4-a67c-65638d89ca28"),sQuery(id+"F21.wireOp",EDGE,"db10adcf-b82a-494a-88b6-329b53716a3a"),sQuery(id+"F21.wireOp",EDGE,"b9fbd47a-e49c-4495-8723-ac3fbff32311"),sQuery(id+"F21.wireOp",EDGE,"8dabacf5-17c3-417d-8f78-b641a870861f"),sQuery(id+"F21.wireOp",EDGE,"fcf0fd75-d0d7-4dab-8f79-4d4778d3e675"),sQuery(id+"F21.wireOp",EDGE,"E280"),sQuery(id+"F21.wireOp",EDGE,"E281"),sQuery(id+"F21.wireOp",EDGE,"E282"),sQuery(id+"F21.wireOp",EDGE,"E283"),sQuery(id+"F21.wireOp",EDGE,"E284"),sQuery(id+"F21.wireOp",EDGE,"E285"),sQuery(id+"F21.wireOp",EDGE,"E286"),sQuery(id+"F21.wireOp",EDGE,"E287"),sQuery(id+"F21.wireOp",EDGE,"E288"),sQuery(id+"F21.wireOp",EDGE,"E289"),sQuery(id+"F21.wireOp",EDGE,"E290"),sQuery(id+"F21.wireOp",EDGE,"E291"),sQuery(id+"F21.wireOp",EDGE,"E292"),sQuery(id+"F21.wireOp",EDGE,"ebf093c5-8378-4633-951f-f2eec86221e3"),sQuery(id+"F21.wireOp",EDGE,"9f0a3954-0cf7-4347-a878-33259e47c607.0.MirrorCS"),sQuery(id+"F21.wireOp",EDGE,"e82cab41-5346-4473-9eb8-a8eaaf8469eb.0.MirrorCS"),sQuery(id+"F21.wireOp",EDGE,"9a93124c-74a7-4b5d-8c4c-b8668731151c.0.MirrorCS"),sQuery(id+"F21.wireOp",EDGE,"1fcc5e95-89ed-40ac-84cd-f24f156d791a.0.MirrorCS"),sQuery(id+"F21.wireOp",EDGE,"E294.0.MirrorCS"),sQuery(id+"F21.wireOp",EDGE,"E295.0.MirrorCS"),sQuery(id+"F21.wireOp",EDGE,"E296.0.MirrorCS"),sQuery(id+"F21.wireOp",EDGE,"E297.0.MirrorCS"),sQuery(id+"F21.wireOp",EDGE,"E298.0.MirrorCS"),sQuery(id+"F21.wireOp",EDGE,"E299.0.MirrorCS"),sQuery(id+"F21.wireOp",EDGE,"E300.0.MirrorCS"),sQuery(id+"F21.wireOp",EDGE,"E301.0.MirrorCS"),sQuery(id+"F21.wireOp",EDGE,"E302.0.MirrorCS"),sQuery(id+"F21.wireOp",EDGE,"E303.0.MirrorCS"),sQuery(id+"F21.wireOp",EDGE,"E304.0.MirrorCS"),sQuery(id+"F21.wireOp",EDGE,"E305.0.MirrorCS"),sQuery(id+"F21.wireOp",EDGE,"E306.0.MirrorCS"),sQuery(id+"F21.wireOp",EDGE,"a0ca25f8-5d4e-4089-912c-7ba0986a8333.0.MirrorCS"),sQuery(id+"F21.wireOp",EDGE,"3ac38a5c-d067-4579-af28-e84971629303.0.MirrorCS")])]});
            var Q1;
            Q1=qCreatedBy(id+"F23.planeOp",FACE);
            mirror(context, id + "F24", {"entities" : qUnion([Q0]), "mirrorPlane" : qUnion([Q1])});
        }
        {
            var Q0;
            Q0=makeQuery(id+"F15.opExtrude","SWEPT_FACE",FACE,{"disambiguationData":[OSD([sQuery(id+"F14.wireOp",EDGE,"E209.right")])]});
            var sketch = newSketch(context, id + "F25", { "sketchPlane" : qUnion([Q0])});
            skLineSegment(sketch, "E330", {"start": v(-93.5, -465.84) * mm, "end": v(-93.5, -475.84) * mm});
            skLineSegment(sketch, "E331", {"start": v(-93.5, -475.84) * mm, "end": v(-99.5, -475.84) * mm});
            skLineSegment(sketch, "E332", {"start": v(-99.5, -475.84) * mm, "end": v(-99.5, -515.84) * mm});
            skLineSegment(sketch, "E333", {"start": v(-99.5, -515.84) * mm, "end": v(-93.5, -515.84) * mm});
            skLineSegment(sketch, "E334", {"start": v(-93.5, -515.84) * mm, "end": v(-93.5, -535.84) * mm});
            skLineSegment(sketch, "E335", {"start": v(-93.5, -535.84) * mm, "end": v(-99.5, -535.84) * mm});
            skLineSegment(sketch, "E336", {"start": v(-99.5, -535.84) * mm, "end": v(-99.5, -575.84) * mm});
            skLineSegment(sketch, "E337", {"start": v(-99.5, -575.84) * mm, "end": v(-93.5, -575.84) * mm});
            skLineSegment(sketch, "E338", {"start": v(-93.5, -575.84) * mm, "end": v(-93.5, -585.84) * mm});
            skLineSegment(sketch, "E339", {"start": v(-93.5, -585.84) * mm, "end": v(-36.5, -585.84) * mm});
            skLineSegment(sketch, "E340", {"start": v(-36.5, -585.84) * mm, "end": v(-36.5, -575.84) * mm});
            skLineSegment(sketch, "E341", {"start": v(-36.5, -575.84) * mm, "end": v(-30.5, -575.84) * mm});
            skLineSegment(sketch, "E342", {"start": v(-30.5, -575.84) * mm, "end": v(-30.5, -535.84) * mm});
            skLineSegment(sketch, "E343", {"start": v(-30.5, -535.84) * mm, "end": v(-36.5, -535.84) * mm});
            skLineSegment(sketch, "E344", {"start": v(-36.5, -535.84) * mm, "end": v(-36.5, -515.84) * mm});
            skLineSegment(sketch, "E345", {"start": v(-36.5, -515.84) * mm, "end": v(-30.5, -515.84) * mm});
            skLineSegment(sketch, "E346", {"start": v(-30.5, -515.84) * mm, "end": v(-30.5, -475.84) * mm});
            skLineSegment(sketch, "E347", {"start": v(-30.5, -475.84) * mm, "end": v(-36.5, -475.84) * mm});
            skLineSegment(sketch, "E348", {"start": v(-36.5, -475.84) * mm, "end": v(-36.5, -465.84) * mm});
            skLineSegment(sketch, "E349", {"start": v(-36.5, -465.84) * mm, "end": v(-93.5, -465.84) * mm});
            skSolve(sketch);
        }
        {
            var Q0;
            Q0 = qSketchRegion(id + "F25", true);
            extrude(context, id + "F26", {"entities" : qUnion([Q0]), "depth" : 6 * mm});
        }
        {
            var Q0;
            Q0=makeQuery(id+"F26.opExtrude","SWEPT_BODY",BODY,{"disambiguationData":[OSD([sQuery(id+"F25.wireOp",EDGE,"E330"),sQuery(id+"F25.wireOp",EDGE,"E331"),sQuery(id+"F25.wireOp",EDGE,"E332"),sQuery(id+"F25.wireOp",EDGE,"E333"),sQuery(id+"F25.wireOp",EDGE,"E334"),sQuery(id+"F25.wireOp",EDGE,"E335"),sQuery(id+"F25.wireOp",EDGE,"E336"),sQuery(id+"F25.wireOp",EDGE,"E337"),sQuery(id+"F25.wireOp",EDGE,"E338"),sQuery(id+"F25.wireOp",EDGE,"E339"),sQuery(id+"F25.wireOp",EDGE,"E340"),sQuery(id+"F25.wireOp",EDGE,"E341"),sQuery(id+"F25.wireOp",EDGE,"E342"),sQuery(id+"F25.wireOp",EDGE,"E343"),sQuery(id+"F25.wireOp",EDGE,"E344"),sQuery(id+"F25.wireOp",EDGE,"E345"),sQuery(id+"F25.wireOp",EDGE,"E346"),sQuery(id+"F25.wireOp",EDGE,"E347"),sQuery(id+"F25.wireOp",EDGE,"E348"),sQuery(id+"F25.wireOp",EDGE,"E349")])]});
            var Q1;
            Q1=qCreatedBy(id+"F23.planeOp",FACE);
            mirror(context, id + "F27", {"entities" : qUnion([Q0]), "mirrorPlane" : qUnion([Q1])});
        }
        {
            var Q0;
            Q0=makeQuery(id+"F15.opExtrude","CAP_FACE",FACE,{"disambiguationData":[OSD([sQuery(id+"F14.wireOp",EDGE,"E197.bottom"),sQuery(id+"F14.wireOp",EDGE,"E197.top"),sQuery(id+"F14.wireOp",EDGE,"E197.left"),sQuery(id+"F14.wireOp",EDGE,"E197.right"),sQuery(id+"F14.wireOp",EDGE,"E198"),sQuery(id+"F14.wireOp",EDGE,"E199"),sQuery(id+"F14.wireOp",EDGE,"E200"),sQuery(id+"F14.wireOp",EDGE,"E201.trimOffspring"),sQuery(id+"F14.wireOp",EDGE,"E202"),sQuery(id+"F14.wireOp",EDGE,"E203"),sQuery(id+"F14.wireOp",EDGE,"E204"),sQuery(id+"F14.wireOp",EDGE,"E205.trimOffspring"),sQuery(id+"F14.wireOp",EDGE,"E206.0"),sQuery(id+"F14.wireOp",EDGE,"E207.bottom"),sQuery(id+"F14.wireOp",EDGE,"E207.top"),sQuery(id+"F14.wireOp",EDGE,"E207.left"),sQuery(id+"F14.wireOp",EDGE,"E207.right"),sQuery(id+"F14.wireOp",EDGE,"E208.bottom"),sQuery(id+"F14.wireOp",EDGE,"E208.top"),sQuery(id+"F14.wireOp",EDGE,"E208.left"),sQuery(id+"F14.wireOp",EDGE,"E208.right"),sQuery(id+"F14.wireOp",EDGE,"E209.bottom"),sQuery(id+"F14.wireOp",EDGE,"E209.top"),sQuery(id+"F14.wireOp",EDGE,"E209.left"),sQuery(id+"F14.wireOp",EDGE,"E209.right"),sQuery(id+"F14.wireOp",EDGE,"E210.bottom"),sQuery(id+"F14.wireOp",EDGE,"E210.top"),sQuery(id+"F14.wireOp",EDGE,"E210.left"),sQuery(id+"F14.wireOp",EDGE,"E210.right"),sQuery(id+"F14.wireOp",EDGE,"E211.0"),sQuery(id+"F14.wireOp",EDGE,"E211.1"),sQuery(id+"F14.wireOp",EDGE,"E211.2"),sQuery(id+"F14.wireOp",EDGE,"E211.3"),sQuery(id+"F14.wireOp",EDGE,"E211.4"),sQuery(id+"F14.wireOp",EDGE,"E211.5"),sQuery(id+"F14.wireOp",EDGE,"E211.6"),sQuery(id+"F14.wireOp",EDGE,"E211.7"),sQuery(id+"F14.wireOp",EDGE,"E212.0"),sQuery(id+"F14.wireOp",EDGE,"E212.1"),sQuery(id+"F14.wireOp",EDGE,"E212.2"),sQuery(id+"F14.wireOp",EDGE,"E212.3"),sQuery(id+"F14.wireOp",EDGE,"E212.4"),sQuery(id+"F14.wireOp",EDGE,"E212.5"),sQuery(id+"F14.wireOp",EDGE,"E212.6"),sQuery(id+"F14.wireOp",EDGE,"E212.7"),sQuery(id+"F14.wireOp",EDGE,"E225.bottom"),sQuery(id+"F14.wireOp",EDGE,"E225.top"),sQuery(id+"F14.wireOp",EDGE,"E225.left"),sQuery(id+"F14.wireOp",EDGE,"E225.right")])],"isStart":true});
            var sketch = newSketch(context, id + "F28", { "sketchPlane" : qUnion([Q0])});
            skCircle(sketch, "E350.0", {"center": v(395, -356.84) * mm, "radius": 1.5 * mm});
            skCircle(sketch, "E350.1", {"center": v(410.5, -363.84) * mm, "radius": 6 * mm});
            skCircle(sketch, "E350.2", {"center": v(402.75, -343.42) * mm, "radius": 1.5 * mm});
            skCircle(sketch, "E350.3", {"center": v(418.25, -343.42) * mm, "radius": 1.5 * mm});
            skCircle(sketch, "E350.4", {"center": v(426, -356.84) * mm, "radius": 1.5 * mm});
            skCircle(sketch, "E350.5", {"center": v(418.25, -370.26) * mm, "radius": 1.5 * mm});
            skCircle(sketch, "E350.6", {"center": v(402.75, -370.26) * mm, "radius": 1.5 * mm});
            skLineSegment(sketch, "E351.rect.bottom", {"start": v(388, -321.84) * mm, "end": v(433, -321.84) * mm});
            skLineSegment(sketch, "E351.rect.top", {"start": v(388, -391.84) * mm, "end": v(433, -391.84) * mm});
            skLineSegment(sketch, "E351.rect.left", {"start": v(388, -321.84) * mm, "end": v(388, -391.84) * mm});
            skLineSegment(sketch, "E351.rect.right", {"start": v(433, -321.84) * mm, "end": v(433, -391.84) * mm});
            skPoint(sketch, "E351.rect.middle", {"position": v(410.5, -356.84) * mm});
            skArc(sketch, "E352", {"start": v(413, -325.84) * mm, "mid": v(410.5, -323.34) * mm, "end": v(408, -325.84) * mm});
            skArc(sketch, "E353", {"start": v(408, -333.34) * mm, "mid": v(410.5, -335.84) * mm, "end": v(413, -333.34) * mm});
            skLineSegment(sketch, "E354", {"start": v(408, -325.84) * mm, "end": v(408, -333.34) * mm});
            skLineSegment(sketch, "E355", {"start": v(413, -325.84) * mm, "end": v(413, -333.34) * mm});
            skLineSegment(sketch, "E356", {"start": v(410.5, -325.84) * mm, "end": v(410.5, -333.34) * mm, "construction": true});
            skPoint(sketch, "E357", {"position": v(410.5, -329.6) * mm});
            skLineSegment(sketch, "E358", {"start": v(395, -356.84) * mm, "end": v(426, -356.84) * mm, "construction": true});
            skLineSegment(sketch, "E359.0.MirrorCS", {"start": v(408, -387.84) * mm, "end": v(408, -380.34) * mm});
            skArc(sketch, "E360.0.MirrorCS", {"start": v(413, -387.84) * mm, "mid": v(410.5, -390.34) * mm, "end": v(408, -387.84) * mm});
            skLineSegment(sketch, "E361.0.MirrorCS", {"start": v(413, -387.84) * mm, "end": v(413, -380.34) * mm});
            skArc(sketch, "E362.0.MirrorCS", {"start": v(408, -380.34) * mm, "mid": v(410.5, -377.84) * mm, "end": v(413, -380.34) * mm});
            skSolve(sketch);
        }
        {
            var Q0;
            Q0 = qSketchRegion(id + "F28", true);
            extrude(context, id + "F29", {"entities" : qUnion([Q0]), "oppositeDirection" : true, "depth" : 6 * mm});
        }
        {
            var Q0;
            Q0=makeQuery(id+"F15.opExtrude","CAP_FACE",FACE,{"disambiguationData":[OSD([sQuery(id+"F14.wireOp",EDGE,"E197.bottom"),sQuery(id+"F14.wireOp",EDGE,"E197.top"),sQuery(id+"F14.wireOp",EDGE,"E197.left"),sQuery(id+"F14.wireOp",EDGE,"E197.right"),sQuery(id+"F14.wireOp",EDGE,"E198"),sQuery(id+"F14.wireOp",EDGE,"E199"),sQuery(id+"F14.wireOp",EDGE,"E200"),sQuery(id+"F14.wireOp",EDGE,"E201.trimOffspring"),sQuery(id+"F14.wireOp",EDGE,"E202"),sQuery(id+"F14.wireOp",EDGE,"E203"),sQuery(id+"F14.wireOp",EDGE,"E204"),sQuery(id+"F14.wireOp",EDGE,"E205.trimOffspring"),sQuery(id+"F14.wireOp",EDGE,"E206.0"),sQuery(id+"F14.wireOp",EDGE,"E207.bottom"),sQuery(id+"F14.wireOp",EDGE,"E207.top"),sQuery(id+"F14.wireOp",EDGE,"E207.left"),sQuery(id+"F14.wireOp",EDGE,"E207.right"),sQuery(id+"F14.wireOp",EDGE,"E208.bottom"),sQuery(id+"F14.wireOp",EDGE,"E208.top"),sQuery(id+"F14.wireOp",EDGE,"E208.left"),sQuery(id+"F14.wireOp",EDGE,"E208.right"),sQuery(id+"F14.wireOp",EDGE,"E209.bottom"),sQuery(id+"F14.wireOp",EDGE,"E209.top"),sQuery(id+"F14.wireOp",EDGE,"E209.left"),sQuery(id+"F14.wireOp",EDGE,"E209.right"),sQuery(id+"F14.wireOp",EDGE,"E210.bottom"),sQuery(id+"F14.wireOp",EDGE,"E210.top"),sQuery(id+"F14.wireOp",EDGE,"E210.left"),sQuery(id+"F14.wireOp",EDGE,"E210.right"),sQuery(id+"F14.wireOp",EDGE,"E211.0"),sQuery(id+"F14.wireOp",EDGE,"E211.1"),sQuery(id+"F14.wireOp",EDGE,"E211.2"),sQuery(id+"F14.wireOp",EDGE,"E211.3"),sQuery(id+"F14.wireOp",EDGE,"E211.4"),sQuery(id+"F14.wireOp",EDGE,"E211.5"),sQuery(id+"F14.wireOp",EDGE,"E211.6"),sQuery(id+"F14.wireOp",EDGE,"E211.7"),sQuery(id+"F14.wireOp",EDGE,"E212.0"),sQuery(id+"F14.wireOp",EDGE,"E212.1"),sQuery(id+"F14.wireOp",EDGE,"E212.2"),sQuery(id+"F14.wireOp",EDGE,"E212.3"),sQuery(id+"F14.wireOp",EDGE,"E212.4"),sQuery(id+"F14.wireOp",EDGE,"E212.5"),sQuery(id+"F14.wireOp",EDGE,"E212.6"),sQuery(id+"F14.wireOp",EDGE,"E212.7"),sQuery(id+"F14.wireOp",EDGE,"E225.bottom"),sQuery(id+"F14.wireOp",EDGE,"E225.top"),sQuery(id+"F14.wireOp",EDGE,"E225.left"),sQuery(id+"F14.wireOp",EDGE,"E225.right"),sQuery(id+"F14.wireOp",EDGE,"E227"),sQuery(id+"F14.wireOp",EDGE,"E228"),sQuery(id+"F14.wireOp",EDGE,"E229"),sQuery(id+"F14.wireOp",EDGE,"E230")])],"isStart":true});
            var sketch = newSketch(context, id + "F30", { "sketchPlane" : qUnion([Q0])});
            skLineSegment(sketch, "E363.bottom", {"start": v(372.5, -323.34) * mm, "end": v(448.5, -323.34) * mm});
            skLineSegment(sketch, "E363.top", {"start": v(372.5, -335.84) * mm, "end": v(388, -335.84) * mm});
            skLineSegment(sketch, "E363.left", {"start": v(372.5, -323.34) * mm, "end": v(372.5, -335.84) * mm});
            skLineSegment(sketch, "E363.right", {"start": v(448.5, -323.34) * mm, "end": v(448.5, -335.84) * mm});
            skCircle(sketch, "E364.0", {"center": v(383, -332.1) * mm, "radius": 2.5 * mm});
            skCircle(sketch, "E364.1", {"center": v(438, -332.1) * mm, "radius": 2.5 * mm});
            skLineSegment(sketch, "E365.bottom", {"start": v(372.5, -377.84) * mm, "end": v(448.5, -377.84) * mm});
            skLineSegment(sketch, "E365.top", {"start": v(372.5, -390.34) * mm, "end": v(448.5, -390.34) * mm});
            skLineSegment(sketch, "E365.left", {"start": v(372.5, -377.84) * mm, "end": v(372.5, -390.34) * mm});
            skLineSegment(sketch, "E365.right", {"start": v(448.5, -377.84) * mm, "end": v(448.5, -390.34) * mm});
            skCircle(sketch, "E366.0", {"center": v(383, -381.6) * mm, "radius": 2.5 * mm});
            skCircle(sketch, "E366.1", {"center": v(438, -381.6) * mm, "radius": 2.5 * mm});
            skCircle(sketch, "E367", {"center": v(410.5, -327.84) * mm, "radius": 2.5 * mm});
            skCircle(sketch, "E368", {"center": v(410.5, -382.34) * mm, "radius": 2.5 * mm});
            skArc(sketch, "E369", {"start": v(433, -335.84) * mm, "mid": v(410.5, -332.34) * mm, "end": v(388, -335.84) * mm});
            skPoint(sketch, "E370", {"position": v(410.5, -332.34) * mm});
            skLineSegment(sketch, "E371.trimOffspring", {"start": v(433, -335.84) * mm, "end": v(448.5, -335.84) * mm});
            skSolve(sketch);
        }
        {
            var Q0;
            Q0 = qSketchRegion(id + "F30", true);
            extrude(context, id + "F31", {"entities" : qUnion([Q0]), "depth" : 6 * mm});
        }
        {
            var Q0;
            Q0=makeQuery(id+"F15.opExtrude","SWEPT_FACE",FACE,{"disambiguationData":[OSD([sQuery(id+"F14.wireOp",EDGE,"E232.1")])]});
            var sketch = newSketch(context, id + "F32", { "sketchPlane" : qUnion([Q0])});
            skLineSegment(sketch, "E372", {"start": v(-93.5, 374.16) * mm, "end": v(-99.5, 374.16) * mm});
            skLineSegment(sketch, "E373", {"start": v(-99.5, 374.16) * mm, "end": v(-99.5, 314.16) * mm});
            skLineSegment(sketch, "E374", {"start": v(-99.5, 314.16) * mm, "end": v(-93.5, 314.16) * mm});
            skLineSegment(sketch, "E375", {"start": v(-93.5, 314.16) * mm, "end": v(-93.5, 234.16) * mm});
            skLineSegment(sketch, "E376", {"start": v(-93.5, 234.16) * mm, "end": v(-99.5, 234.16) * mm});
            skLineSegment(sketch, "E377", {"start": v(-99.5, 234.16) * mm, "end": v(-99.5, 174.16) * mm});
            skLineSegment(sketch, "E378", {"start": v(-99.5, 174.16) * mm, "end": v(-93.5, 174.16) * mm});
            skLineSegment(sketch, "E379", {"start": v(-93.5, 174.16) * mm, "end": v(-93.5, 94.16) * mm});
            skLineSegment(sketch, "E380", {"start": v(-93.5, 94.16) * mm, "end": v(-99.5, 94.16) * mm});
            skLineSegment(sketch, "E381", {"start": v(-99.5, 94.16) * mm, "end": v(-99.5, 34.16) * mm});
            skLineSegment(sketch, "E382", {"start": v(-99.5, 34.16) * mm, "end": v(-93.5, 34.16) * mm});
            skLineSegment(sketch, "E383", {"start": v(-93.5, 34.16) * mm, "end": v(-93.5, -45.84) * mm});
            skLineSegment(sketch, "E384", {"start": v(-93.5, -45.84) * mm, "end": v(-99.5, -45.84) * mm});
            skLineSegment(sketch, "E385", {"start": v(-99.5, -45.84) * mm, "end": v(-99.5, -105.84) * mm});
            skLineSegment(sketch, "E386", {"start": v(-99.5, -105.84) * mm, "end": v(-93.5, -105.84) * mm});
            skLineSegment(sketch, "E387", {"start": v(-93.5, -105.84) * mm, "end": v(-93.5, -185.84) * mm});
            skLineSegment(sketch, "E388", {"start": v(-93.5, -185.84) * mm, "end": v(-99.5, -185.84) * mm});
            skLineSegment(sketch, "E389", {"start": v(-99.5, -185.84) * mm, "end": v(-99.5, -245.84) * mm});
            skLineSegment(sketch, "E390", {"start": v(-99.5, -245.84) * mm, "end": v(-93.5, -245.84) * mm});
            skLineSegment(sketch, "E391", {"start": v(-93.5, -245.84) * mm, "end": v(-93.5, -269.84) * mm});
            skLineSegment(sketch, "E392", {"start": v(-93.5, -269.84) * mm, "end": v(-65, -269.84) * mm});
            skLineSegment(sketch, "E393", {"start": v(-65, -269.84) * mm, "end": v(-65, 399.16) * mm, "construction": true});
            skLineSegment(sketch, "E394", {"start": v(-65, 399.16) * mm, "end": v(-93.5, 399.16) * mm});
            skLineSegment(sketch, "E395", {"start": v(-93.5, 399.16) * mm, "end": v(-93.5, 374.16) * mm});
            skLineSegment(sketch, "E396", {"start": v(-65, 399.16) * mm, "end": v(-36.5, 399.16) * mm, "construction": true});
            skLineSegment(sketch, "E397.0.MirrorCS", {"start": v(-65, 399.16) * mm, "end": v(-36.5, 399.16) * mm});
            skLineSegment(sketch, "E398.0.MirrorCS", {"start": v(-36.5, 399.16) * mm, "end": v(-36.5, 374.16) * mm});
            skLineSegment(sketch, "E399.0.MirrorCS", {"start": v(-36.5, 374.16) * mm, "end": v(-30.5, 374.16) * mm});
            skLineSegment(sketch, "E400.0.MirrorCS", {"start": v(-30.5, 374.16) * mm, "end": v(-30.5, 314.16) * mm});
            skLineSegment(sketch, "E401.0.MirrorCS", {"start": v(-30.5, 314.16) * mm, "end": v(-36.5, 314.16) * mm});
            skLineSegment(sketch, "E402.0.MirrorCS", {"start": v(-36.5, 314.16) * mm, "end": v(-36.5, 234.16) * mm});
            skLineSegment(sketch, "E403.0.MirrorCS", {"start": v(-36.5, 234.16) * mm, "end": v(-30.5, 234.16) * mm});
            skLineSegment(sketch, "E404.0.MirrorCS", {"start": v(-30.5, 234.16) * mm, "end": v(-30.5, 174.16) * mm});
            skLineSegment(sketch, "E405.0.MirrorCS", {"start": v(-30.5, 174.16) * mm, "end": v(-36.5, 174.16) * mm});
            skLineSegment(sketch, "E406.0.MirrorCS", {"start": v(-36.5, 174.16) * mm, "end": v(-36.5, 94.16) * mm});
            skLineSegment(sketch, "E407.0.MirrorCS", {"start": v(-36.5, 94.16) * mm, "end": v(-30.5, 94.16) * mm});
            skLineSegment(sketch, "E408.0.MirrorCS", {"start": v(-30.5, 94.16) * mm, "end": v(-30.5, 34.16) * mm});
            skLineSegment(sketch, "E409.0.MirrorCS", {"start": v(-30.5, 34.16) * mm, "end": v(-36.5, 34.16) * mm});
            skLineSegment(sketch, "E410.0.MirrorCS", {"start": v(-36.5, 34.16) * mm, "end": v(-36.5, -45.84) * mm});
            skLineSegment(sketch, "E411.0.MirrorCS", {"start": v(-36.5, -45.84) * mm, "end": v(-30.5, -45.84) * mm});
            skLineSegment(sketch, "E412.0.MirrorCS", {"start": v(-30.5, -45.84) * mm, "end": v(-30.5, -105.84) * mm});
            skLineSegment(sketch, "E413.0.MirrorCS", {"start": v(-30.5, -105.84) * mm, "end": v(-36.5, -105.84) * mm});
            skLineSegment(sketch, "E414.0.MirrorCS", {"start": v(-36.5, -105.84) * mm, "end": v(-36.5, -185.84) * mm});
            skLineSegment(sketch, "E415.0.MirrorCS", {"start": v(-36.5, -185.84) * mm, "end": v(-30.5, -185.84) * mm});
            skLineSegment(sketch, "E416.0.MirrorCS", {"start": v(-30.5, -185.84) * mm, "end": v(-30.5, -245.84) * mm});
            skLineSegment(sketch, "E417.0.MirrorCS", {"start": v(-30.5, -245.84) * mm, "end": v(-36.5, -245.84) * mm});
            skLineSegment(sketch, "E418.0.MirrorCS", {"start": v(-36.5, -245.84) * mm, "end": v(-36.5, -269.84) * mm});
            skLineSegment(sketch, "E419.0.MirrorCS", {"start": v(-36.5, -269.84) * mm, "end": v(-65, -269.84) * mm});
            skSolve(sketch);
        }
        {
            var Q0;
            Q0 = qSketchRegion(id + "F32", true);
            extrude(context, id + "F33", {"entities" : qUnion([Q0]), "depth" : 6 * mm});
        }
    });
